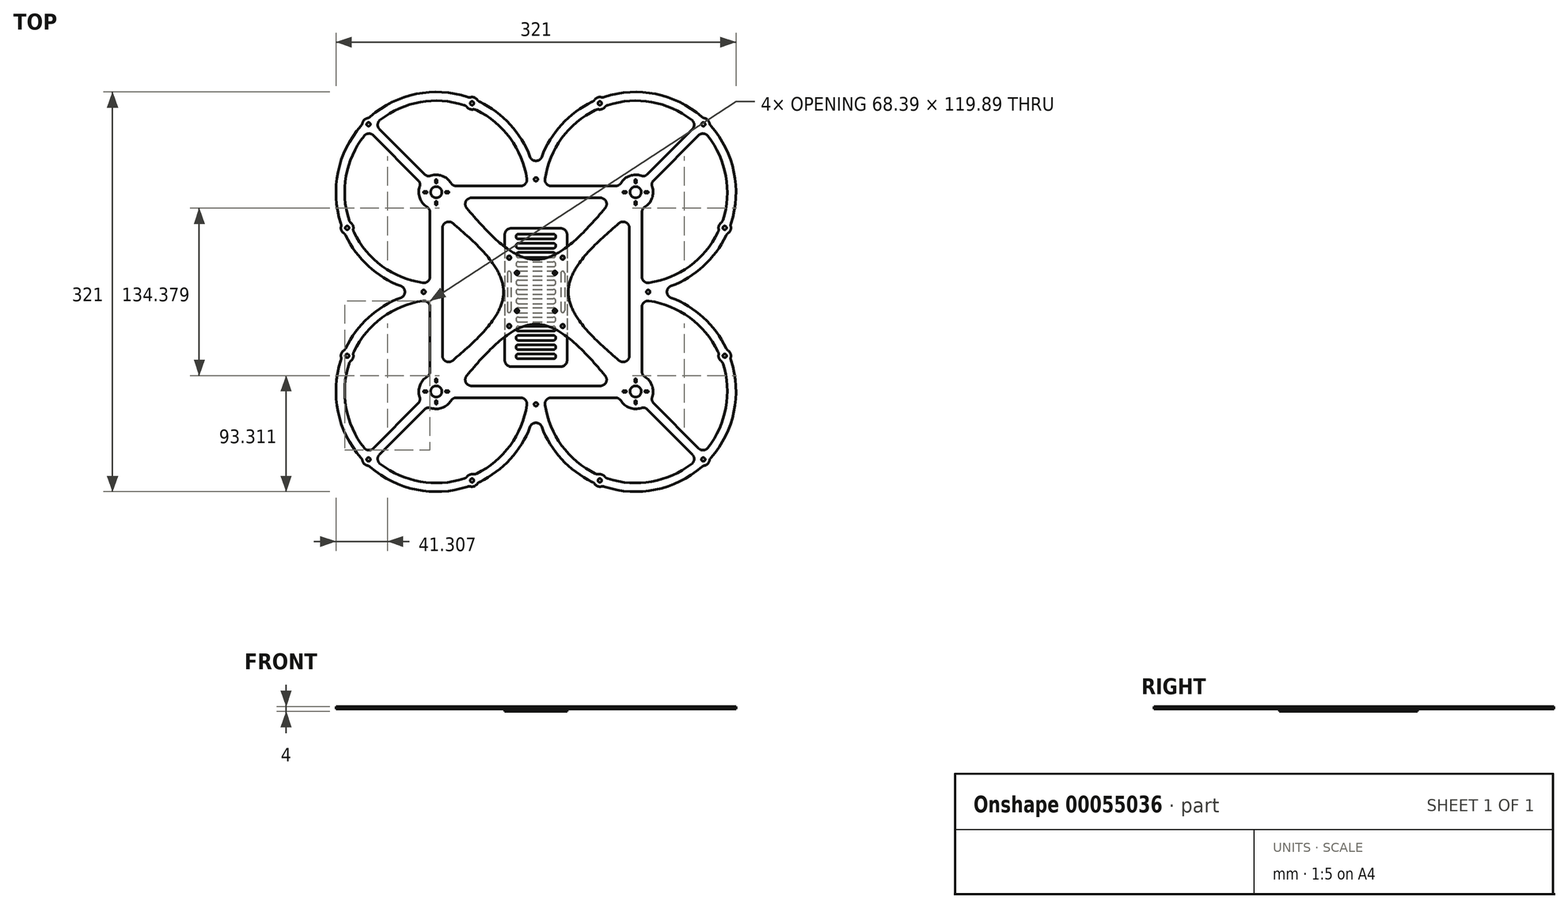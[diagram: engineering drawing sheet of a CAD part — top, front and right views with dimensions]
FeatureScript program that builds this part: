
annotation { "Feature Type Name" : "Feature", "Feature Type Description" : "" }
export const myFeature = defineFeature(function(context is Context, id is Id, definition is map)
    precondition{}
    {
        {
            var Q0;
            Q0=qCreatedBy(makeId("Top.planeOp"),FACE);
            var sketch = newSketch(context, id + "F0", { "sketchPlane" : qUnion([Q0])});
            skPoint(sketch, "E0.rect.middle", {"position": v(0, 0) * mm});
            skArc(sketch, "E1", {"start": v(-68.1, 87.37) * mm, "mid": v(-75.23, 93.16) * mm, "end": v(-84.42, 93.28) * mm});
            skArc(sketch, "E2", {"start": v(87.37, 68.1) * mm, "mid": v(93.16, 75.24) * mm, "end": v(93.28, 84.43) * mm});
            skArc(sketch, "E3", {"start": v(80, -66) * mm, "mid": v(79.97, -66) * mm, "end": v(79.94, -66) * mm});
            skArc(sketch, "E4", {"start": v(-87.37, -68.1) * mm, "mid": v(-93.16, -75.24) * mm, "end": v(-93.28, -84.43) * mm});
            skLineSegment(sketch, "E5.rect.bottom", {"start": v(15.25, -15.25) * mm, "end": v(-15.25, -15.25) * mm, "construction": true});
            skLineSegment(sketch, "E5.rect.top", {"start": v(15.25, 15.25) * mm, "end": v(-15.25, 15.25) * mm, "construction": true});
            skLineSegment(sketch, "E5.rect.left", {"start": v(15.25, -15.25) * mm, "end": v(15.25, 15.25) * mm, "construction": true});
            skLineSegment(sketch, "E5.rect.right", {"start": v(-15.25, -15.25) * mm, "end": v(-15.25, 15.25) * mm, "construction": true});
            skCircle(sketch, "E6", {"center": v(-80, 80) * mm, "radius": 63.5 * mm, "construction": true});
            skCircle(sketch, "E7", {"center": v(80, 80) * mm, "radius": 63.5 * mm, "construction": true});
            skCircle(sketch, "E8", {"center": v(-80, -80) * mm, "radius": 63.5 * mm, "construction": true});
            skCircle(sketch, "E9", {"center": v(80, -80) * mm, "radius": 63.5 * mm, "construction": true});
            skLineSegment(sketch, "E10.rect.bottom", {"start": v(26, -26) * mm, "end": v(-26, -26) * mm});
            skLineSegment(sketch, "E10.rect.top", {"start": v(26, 26) * mm, "end": v(-26, 26) * mm});
            skLineSegment(sketch, "E10.rect.left", {"start": v(26, -26) * mm, "end": v(26, 26) * mm});
            skLineSegment(sketch, "E10.rect.right", {"start": v(-26, -26) * mm, "end": v(-26, 26) * mm});
            skLineSegment(sketch, "E11.0", {"start": v(-85, -63.84) * mm, "end": v(-85, -12.23) * mm});
            skLineSegment(sketch, "E11.1", {"start": v(63.84, -85) * mm, "end": v(12.23, -85) * mm});
            skLineSegment(sketch, "E11.2", {"start": v(85, -63.84) * mm, "end": v(85, -12.23) * mm});
            skLineSegment(sketch, "E11.3", {"start": v(63.84, 85) * mm, "end": v(12.23, 85) * mm});
            skLineSegment(sketch, "E12.0", {"start": v(51.72, 75.5) * mm, "end": v(-51.72, 75.5) * mm});
            skLineSegment(sketch, "E12.1", {"start": v(75, -51.34) * mm, "end": v(75, 51.3) * mm});
            skLineSegment(sketch, "E12.2", {"start": v(51.72, -75.5) * mm, "end": v(-51.72, -75.5) * mm});
            skLineSegment(sketch, "E12.3", {"start": v(-75, -51.3) * mm, "end": v(-75, 51.3) * mm});
            skFitSpline(sketch, "E13", {"points": [v(-66, 80) * mm, v(0, 26) * mm, v(66, 80) * mm], "startDerivative": vector(132, -162) * mm, "endDerivative": vector(132, 162) * mm});
            skFitSpline(sketch, "E14", {"points": [v(-80, 66) * mm, v(-26, 0) * mm, v(-80, -66) * mm], "startDerivative": vector(162, -132) * mm, "endDerivative": vector(-162, -132) * mm});
            skFitSpline(sketch, "E15", {"points": [v(-66, -80) * mm, v(0, -26) * mm, v(66, -80) * mm], "startDerivative": vector(132, 162) * mm, "endDerivative": vector(132, -162) * mm});
            skFitSpline(sketch, "E16", {"points": [v(79.94, -66) * mm, v(26, 0) * mm, v(80, 66) * mm], "startDerivative": vector(-161.86, 132.02) * mm, "endDerivative": vector(161.96, 131.98) * mm});
            skArc(sketch, "E17.trimOffspring", {"start": v(68.1, -87.37) * mm, "mid": v(75.23, -93.16) * mm, "end": v(84.42, -93.28) * mm});
            skPoint(sketch, "E18", {"position": v(0, -124.8) * mm});
            skPoint(sketch, "E19.orphan", {"position": v(0, 114.1) * mm});
            skLineSegment(sketch, "E20.trimOffspring", {"start": v(-85, 12.23) * mm, "end": v(-85, 63.84) * mm});
            skLineSegment(sketch, "E21.trimOffspring", {"start": v(85, 12.23) * mm, "end": v(85, 63.84) * mm});
            skLineSegment(sketch, "E22.trimOffspring", {"start": v(-12.23, -85) * mm, "end": v(-63.84, -85) * mm});
            skLineSegment(sketch, "E23.trimOffspring", {"start": v(-12.23, 85) * mm, "end": v(-63.84, 85) * mm});
            skLineSegment(sketch, "E24", {"start": v(-124.66, 124.8) * mm, "end": v(-125, 125.15) * mm, "construction": true});
            skLineSegment(sketch, "E25", {"start": v(124.66, 124.8) * mm, "end": v(124.83, 124.97) * mm, "construction": true});
            skLineSegment(sketch, "E26", {"start": v(124.66, -124.8) * mm, "end": v(124.83, -124.97) * mm, "construction": true});
            skLineSegment(sketch, "E27", {"start": v(-124.66, -124.8) * mm, "end": v(-124.83, -124.97) * mm, "construction": true});
            skLineSegment(sketch, "E28.0", {"start": v(-94.48, 89.54) * mm, "end": v(-130.46, 125.67) * mm});
            skLineSegment(sketch, "E29.0", {"start": v(94.48, 89.54) * mm, "end": v(130.46, 125.67) * mm});
            skLineSegment(sketch, "E30.0", {"start": v(89.54, -94.5) * mm, "end": v(125.5, -130.61) * mm});
            skLineSegment(sketch, "E31.0", {"start": v(-94.48, -89.54) * mm, "end": v(-130.46, -125.67) * mm});
            skLineSegment(sketch, "E32.0", {"start": v(-89.54, 94.5) * mm, "end": v(-125.5, 130.61) * mm});
            skLineSegment(sketch, "E33.0", {"start": v(89.54, 94.5) * mm, "end": v(125.5, 130.61) * mm});
            skLineSegment(sketch, "E34.0", {"start": v(94.48, -89.54) * mm, "end": v(130.46, -125.67) * mm});
            skLineSegment(sketch, "E35.0", {"start": v(-89.54, -94.5) * mm, "end": v(-125.5, -130.61) * mm});
            skPoint(sketch, "E36.orphan", {"position": v(-89.9, 89.9) * mm});
            skPoint(sketch, "E37.orphan", {"position": v(-133.3, 133.48) * mm});
            skPoint(sketch, "E38.orphan", {"position": v(89.9, 89.9) * mm});
            skPoint(sketch, "E39.orphan", {"position": v(131.88, 132.06) * mm});
            skPoint(sketch, "E40.orphan", {"position": v(89.9, -89.9) * mm});
            skPoint(sketch, "E41.orphan", {"position": v(131.88, -132.06) * mm});
            skPoint(sketch, "E42.orphan", {"position": v(-89.9, -89.9) * mm});
            skPoint(sketch, "E43.orphan", {"position": v(-131.88, -132.06) * mm});
            skLineSegment(sketch, "E44", {"start": v(-87.42, 92.37) * mm, "end": v(-87.11, 92.06) * mm});
            skLineSegment(sketch, "E45", {"start": v(-92.38, 87.43) * mm, "end": v(-92.06, 87.1) * mm});
            skLineSegment(sketch, "E46", {"start": v(87.42, 92.37) * mm, "end": v(87.11, 92.06) * mm});
            skLineSegment(sketch, "E47", {"start": v(92.38, 87.43) * mm, "end": v(92.06, 87.1) * mm});
            skLineSegment(sketch, "E48", {"start": v(92.38, -87.43) * mm, "end": v(92.06, -87.1) * mm});
            skLineSegment(sketch, "E49", {"start": v(87.42, -92.37) * mm, "end": v(87.11, -92.06) * mm});
            skLineSegment(sketch, "E50", {"start": v(-92.38, -87.43) * mm, "end": v(-92.06, -87.1) * mm});
            skLineSegment(sketch, "E51", {"start": v(-87.42, -92.37) * mm, "end": v(-87.11, -92.06) * mm});
            skArc(sketch, "E52.trimOffspring", {"start": v(-93.28, 84.43) * mm, "mid": v(-93.16, 75.24) * mm, "end": v(-87.37, 68.1) * mm});
            skArc(sketch, "E53.filletArc", {"start": v(-89.54, 94.5) * mm, "mid": v(-87.15, 93.16) * mm, "end": v(-84.42, 93.28) * mm});
            skArc(sketch, "E54.trimOffspring", {"start": v(84.42, 93.28) * mm, "mid": v(75.23, 93.16) * mm, "end": v(68.1, 87.37) * mm});
            skArc(sketch, "E55.trimOffspring", {"start": v(93.28, -84.43) * mm, "mid": v(93.16, -75.24) * mm, "end": v(87.37, -68.1) * mm});
            skArc(sketch, "E56.trimOffspring", {"start": v(-84.42, -93.28) * mm, "mid": v(-75.23, -93.16) * mm, "end": v(-68.1, -87.37) * mm});
            skArc(sketch, "E57.filletArc", {"start": v(-93.28, 84.43) * mm, "mid": v(-93.16, 87.16) * mm, "end": v(-94.48, 89.54) * mm});
            skPoint(sketch, "E58.visualSharp", {"position": v(-66.92, 85) * mm});
            skArc(sketch, "E58.filletArc", {"start": v(-68.1, 87.37) * mm, "mid": v(-66.28, 85.63) * mm, "end": v(-63.84, 85) * mm});
            skPoint(sketch, "E59.visualSharp", {"position": v(-85, 66.92) * mm});
            skArc(sketch, "E59.filletArc", {"start": v(-85, 63.84) * mm, "mid": v(-85.63, 66.28) * mm, "end": v(-87.37, 68.1) * mm});
            skPoint(sketch, "E60.visualSharp", {"position": v(-62.33, 75.5) * mm});
            skArc(sketch, "E60.filletArc", {"start": v(-51.72, 75.5) * mm, "mid": v(-56.25, 72.62) * mm, "end": v(-55.56, 67.3) * mm});
            skPoint(sketch, "E61.visualSharp", {"position": v(-75, 61.92) * mm});
            skArc(sketch, "E61.filletArc", {"start": v(-66.79, 55.14) * mm, "mid": v(-72.12, 55.84) * mm, "end": v(-75, 51.3) * mm});
            skArc(sketch, "E62.filletArc", {"start": v(-125.02, 138.1) * mm, "mid": v(-126.95, 134.46) * mm, "end": v(-125.5, 130.61) * mm});
            skArc(sketch, "E63.filletArc", {"start": v(-130.46, 125.67) * mm, "mid": v(-134.3, 127.13) * mm, "end": v(-137.94, 125.22) * mm});
            skPoint(sketch, "E64.visualSharp", {"position": v(-4.93, 114.55) * mm});
            skPoint(sketch, "E65.visualSharp", {"position": v(5, 114.56) * mm});
            skPoint(sketch, "E66.visualSharp", {"position": v(66.92, 85) * mm});
            skArc(sketch, "E66.filletArc", {"start": v(63.84, 85) * mm, "mid": v(66.28, 85.63) * mm, "end": v(68.1, 87.37) * mm});
            skArc(sketch, "E67.filletArc", {"start": v(84.42, 93.28) * mm, "mid": v(87.15, 93.16) * mm, "end": v(89.54, 94.5) * mm});
            skArc(sketch, "E68.filletArc", {"start": v(125.5, 130.61) * mm, "mid": v(126.95, 134.46) * mm, "end": v(125.02, 138.1) * mm});
            skArc(sketch, "E69.filletArc", {"start": v(137.94, 125.22) * mm, "mid": v(134.3, 127.13) * mm, "end": v(130.46, 125.67) * mm});
            skArc(sketch, "E70.filletArc", {"start": v(94.48, 89.54) * mm, "mid": v(93.16, 87.16) * mm, "end": v(93.28, 84.43) * mm});
            skPoint(sketch, "E71.visualSharp", {"position": v(85, 66.92) * mm});
            skArc(sketch, "E71.filletArc", {"start": v(87.37, 68.1) * mm, "mid": v(85.63, 66.28) * mm, "end": v(85, 63.84) * mm});
            skPoint(sketch, "E72.visualSharp", {"position": v(62.33, 75.5) * mm});
            skArc(sketch, "E72.filletArc", {"start": v(55.56, 67.3) * mm, "mid": v(56.25, 72.62) * mm, "end": v(51.72, 75.5) * mm});
            skPoint(sketch, "E73.visualSharp", {"position": v(75, 61.92) * mm});
            skArc(sketch, "E73.filletArc", {"start": v(75, 51.3) * mm, "mid": v(72.12, 55.83) * mm, "end": v(66.79, 55.14) * mm});
            skPoint(sketch, "E74.visualSharp", {"position": v(85, -66.92) * mm});
            skArc(sketch, "E74.filletArc", {"start": v(85, -63.84) * mm, "mid": v(85.63, -66.28) * mm, "end": v(87.37, -68.1) * mm});
            skArc(sketch, "E75.filletArc", {"start": v(93.28, -84.43) * mm, "mid": v(93.16, -87.16) * mm, "end": v(94.48, -89.54) * mm});
            skArc(sketch, "E76.filletArc", {"start": v(130.46, -125.67) * mm, "mid": v(134.3, -127.13) * mm, "end": v(137.94, -125.22) * mm});
            skArc(sketch, "E77.filletArc", {"start": v(125.02, -138.1) * mm, "mid": v(126.95, -134.46) * mm, "end": v(125.5, -130.61) * mm});
            skArc(sketch, "E78.filletArc", {"start": v(89.54, -94.5) * mm, "mid": v(87.15, -93.16) * mm, "end": v(84.42, -93.28) * mm});
            skPoint(sketch, "E79.visualSharp", {"position": v(66.92, -85) * mm});
            skArc(sketch, "E79.filletArc", {"start": v(68.1, -87.37) * mm, "mid": v(66.28, -85.63) * mm, "end": v(63.84, -85) * mm});
            skPoint(sketch, "E80.visualSharp", {"position": v(62.33, -75.5) * mm});
            skArc(sketch, "E80.filletArc", {"start": v(51.72, -75.5) * mm, "mid": v(56.25, -72.62) * mm, "end": v(55.56, -67.3) * mm});
            skPoint(sketch, "E81.visualSharp", {"position": v(75, -61.96) * mm});
            skArc(sketch, "E81.filletArc", {"start": v(66.79, -55.17) * mm, "mid": v(72.11, -55.87) * mm, "end": v(75, -51.34) * mm});
            skPoint(sketch, "E82.visualSharp", {"position": v(-5.02, -114.56) * mm});
            skPoint(sketch, "E83.visualSharp", {"position": v(-66.92, -85) * mm});
            skArc(sketch, "E83.filletArc", {"start": v(-63.84, -85) * mm, "mid": v(-66.28, -85.63) * mm, "end": v(-68.1, -87.37) * mm});
            skArc(sketch, "E84.filletArc", {"start": v(-84.42, -93.28) * mm, "mid": v(-87.15, -93.16) * mm, "end": v(-89.54, -94.5) * mm});
            skArc(sketch, "E85.filletArc", {"start": v(-125.5, -130.61) * mm, "mid": v(-126.95, -134.46) * mm, "end": v(-125.02, -138.1) * mm});
            skArc(sketch, "E86.filletArc", {"start": v(-137.94, -125.22) * mm, "mid": v(-134.3, -127.13) * mm, "end": v(-130.46, -125.67) * mm});
            skArc(sketch, "E87.filletArc", {"start": v(-94.48, -89.54) * mm, "mid": v(-93.16, -87.16) * mm, "end": v(-93.28, -84.43) * mm});
            skPoint(sketch, "E88.visualSharp", {"position": v(-85, -66.92) * mm});
            skArc(sketch, "E88.filletArc", {"start": v(-87.37, -68.1) * mm, "mid": v(-85.63, -66.28) * mm, "end": v(-85, -63.84) * mm});
            skPoint(sketch, "E89.visualSharp", {"position": v(-62.33, -75.5) * mm});
            skArc(sketch, "E89.filletArc", {"start": v(-55.56, -67.3) * mm, "mid": v(-56.25, -72.62) * mm, "end": v(-51.72, -75.5) * mm});
            skPoint(sketch, "E90.visualSharp", {"position": v(-75, -61.92) * mm});
            skArc(sketch, "E90.filletArc", {"start": v(-75, -51.3) * mm, "mid": v(-72.12, -55.84) * mm, "end": v(-66.79, -55.14) * mm});
            skArc(sketch, "E91", {"start": v(33.54, -16.78) * mm, "mid": v(37.5, 0) * mm, "end": v(33.54, 16.77) * mm});
            skFitSpline(sketch, "E92.trimOffspring", {"points": [v(-66, -80) * mm, v(0, -26) * mm, v(66, -80) * mm], "startDerivative": vector(132, 162) * mm, "endDerivative": vector(132, -162) * mm});
            skArc(sketch, "E93.trimOffspring", {"start": v(-16.77, -33.54) * mm, "mid": v(0, -37.5) * mm, "end": v(16.77, -33.54) * mm});
            skFitSpline(sketch, "E94.trimOffspring", {"points": [v(-80, 66) * mm, v(-26, 0) * mm, v(-80, -66) * mm], "startDerivative": vector(162, -132) * mm, "endDerivative": vector(-162, -132) * mm});
            skArc(sketch, "E95.trimOffspring", {"start": v(-33.54, 16.77) * mm, "mid": v(-37.5, 0) * mm, "end": v(-33.54, -16.77) * mm});
            skArc(sketch, "E96.trimOffspring", {"start": v(16.77, 33.54) * mm, "mid": v(0, 37.5) * mm, "end": v(-16.77, 33.54) * mm});
            skPoint(sketch, "E97.visualSharp", {"position": v(-19.22, 32.2) * mm});
            skArc(sketch, "E97.filletArc", {"start": v(-21.81, 33.87) * mm, "mid": v(-19.34, 33.02) * mm, "end": v(-16.77, 33.54) * mm});
            skPoint(sketch, "E98.visualSharp", {"position": v(19.22, 32.2) * mm});
            skArc(sketch, "E98.filletArc", {"start": v(16.77, 33.54) * mm, "mid": v(19.34, 33.02) * mm, "end": v(21.81, 33.87) * mm});
            skPoint(sketch, "E99.visualSharp", {"position": v(32.2, 19.22) * mm});
            skArc(sketch, "E99.filletArc", {"start": v(33.87, 21.8) * mm, "mid": v(33.02, 19.34) * mm, "end": v(33.54, 16.77) * mm});
            skPoint(sketch, "E100.visualSharp", {"position": v(32.2, -19.23) * mm});
            skArc(sketch, "E100.filletArc", {"start": v(33.54, -16.78) * mm, "mid": v(33.02, -19.34) * mm, "end": v(33.87, -21.82) * mm});
            skPoint(sketch, "E101.visualSharp", {"position": v(19.22, -32.2) * mm});
            skArc(sketch, "E101.filletArc", {"start": v(21.81, -33.87) * mm, "mid": v(19.34, -33.02) * mm, "end": v(16.77, -33.54) * mm});
            skPoint(sketch, "E102.visualSharp", {"position": v(-19.22, -32.2) * mm});
            skArc(sketch, "E102.filletArc", {"start": v(-16.77, -33.54) * mm, "mid": v(-19.34, -33.02) * mm, "end": v(-21.81, -33.87) * mm});
            skPoint(sketch, "E103.visualSharp", {"position": v(-32.2, -19.22) * mm});
            skArc(sketch, "E103.filletArc", {"start": v(-33.87, -21.81) * mm, "mid": v(-33.02, -19.34) * mm, "end": v(-33.54, -16.77) * mm});
            skPoint(sketch, "E104.visualSharp", {"position": v(-32.2, 19.22) * mm});
            skArc(sketch, "E104.filletArc", {"start": v(-33.54, 16.77) * mm, "mid": v(-33.02, 19.34) * mm, "end": v(-33.87, 21.81) * mm});
            skCircle(sketch, "E105", {"center": v(15.25, -15.25) * mm, "radius": 1.5 * mm});
            skCircle(sketch, "E106", {"center": v(-15.25, -15.25) * mm, "radius": 1.5 * mm});
            skCircle(sketch, "E107", {"center": v(-15.25, 15.25) * mm, "radius": 1.5 * mm});
            skCircle(sketch, "E108", {"center": v(15.25, 15.25) * mm, "radius": 1.5 * mm});
            skCircle(sketch, "E109", {"center": v(32.2, 0) * mm, "radius": 1.5 * mm});
            skCircle(sketch, "E110", {"center": v(0, -32.2) * mm, "radius": 1.5 * mm});
            skLineSegment(sketch, "E111", {"start": v(0, -141.51) * mm, "end": v(0, 75.5) * mm, "construction": true});
            skLineSegment(sketch, "E112", {"start": v(141.95, 0) * mm, "end": v(-75, 0) * mm, "construction": true});
            skCircle(sketch, "E113.MirrorC", {"center": v(-32.2, 0) * mm, "radius": 1.5 * mm});
            skCircle(sketch, "E114.MirrorC", {"center": v(0, 32.2) * mm, "radius": 1.5 * mm});
            skArc(sketch, "E115.filletArc", {"start": v(12.23, -85) * mm, "mid": v(8.45, -86.73) * mm, "end": v(7.29, -90.73) * mm});
            skArc(sketch, "E116.filletArc", {"start": v(-7.29, -90.73) * mm, "mid": v(-8.45, -86.73) * mm, "end": v(-12.23, -85) * mm});
            skArc(sketch, "E117.filletArc", {"start": v(4.68, -108.4) * mm, "mid": v(0, -105.17) * mm, "end": v(-4.68, -108.4) * mm});
            skPoint(sketch, "E118.visualSharp", {"position": v(6.67, 85) * mm});
            skArc(sketch, "E118.filletArc", {"start": v(7.29, 90.73) * mm, "mid": v(8.45, 86.73) * mm, "end": v(12.23, 85) * mm});
            skPoint(sketch, "E119.visualSharp", {"position": v(-6.67, 85) * mm});
            skArc(sketch, "E119.filletArc", {"start": v(-12.23, 85) * mm, "mid": v(-8.45, 86.73) * mm, "end": v(-7.29, 90.73) * mm});
            skPoint(sketch, "E120.visualSharp", {"position": v(0, 88.96) * mm});
            skArc(sketch, "E120.filletArc", {"start": v(-4.68, 108.4) * mm, "mid": v(0, 105.17) * mm, "end": v(4.68, 108.4) * mm});
            skArc(sketch, "E121.filletArc", {"start": v(-85, -12.23) * mm, "mid": v(-86.73, -8.45) * mm, "end": v(-90.73, -7.29) * mm});
            skArc(sketch, "E122.filletArc", {"start": v(-90.73, 7.29) * mm, "mid": v(-86.73, 8.45) * mm, "end": v(-85, 12.23) * mm});
            skPoint(sketch, "E123.visualSharp", {"position": v(-88.96, 0) * mm});
            skArc(sketch, "E123.filletArc", {"start": v(-108.4, -4.68) * mm, "mid": v(-105.17, 0) * mm, "end": v(-108.4, 4.68) * mm});
            skPoint(sketch, "E124.visualSharp", {"position": v(85, -6.67) * mm});
            skArc(sketch, "E124.filletArc", {"start": v(90.73, -7.29) * mm, "mid": v(86.73, -8.45) * mm, "end": v(85, -12.23) * mm});
            skPoint(sketch, "E125.visualSharp", {"position": v(85, 6.67) * mm});
            skArc(sketch, "E125.filletArc", {"start": v(85, 12.23) * mm, "mid": v(86.73, 8.45) * mm, "end": v(90.73, 7.29) * mm});
            skArc(sketch, "E126.filletArc", {"start": v(108.4, 4.68) * mm, "mid": v(105.17, 0) * mm, "end": v(108.4, -4.68) * mm});
            skArc(sketch, "E127", {"start": v(-90.73, 7.29) * mm, "mid": v(-123.42, 20.7) * mm, "end": v(-146.07, 47.8) * mm});
            skArc(sketch, "E128", {"start": v(-108.4, 4.68) * mm, "mid": v(-134.45, 20.7) * mm, "end": v(-152.63, 45.3) * mm});
            skArc(sketch, "E129", {"start": v(-7.29, 90.73) * mm, "mid": v(-20.66, 123.37) * mm, "end": v(-47.7, 146.02) * mm});
            skLineSegment(sketch, "E130", {"start": v(-138.95, 56.4) * mm, "end": v(-148.23, 52.68) * mm, "construction": true});
            skLineSegment(sketch, "E131", {"start": v(-148.23, 52.68) * mm, "end": v(-160.6, 47.73) * mm, "construction": true});
            skLineSegment(sketch, "E132", {"start": v(-52.57, 148.19) * mm, "end": v(-48.09, 159.32) * mm, "construction": true});
            skCircle(sketch, "E133", {"center": v(-80, 80) * mm, "radius": 77 * mm, "construction": true});
            skArc(sketch, "E134", {"start": v(-156.38, 52.4) * mm, "mid": v(-156.13, 49.52) * mm, "end": v(-154.31, 47.26) * mm});
            skArc(sketch, "E135", {"start": v(-55.18, 148.34) * mm, "mid": v(-53.13, 146.8) * mm, "end": v(-50.58, 146.48) * mm});
            skArc(sketch, "E136.trimOffspring", {"start": v(-47.14, 154.26) * mm, "mid": v(-49.4, 156.07) * mm, "end": v(-52.28, 156.33) * mm});
            skArc(sketch, "E137.trimOffspring", {"start": v(-45.17, 152.58) * mm, "mid": v(-20.66, 134.4) * mm, "end": v(-4.68, 108.4) * mm});
            skArc(sketch, "E138.trimOffspring", {"start": v(-57.58, 150) * mm, "mid": v(-92.77, 152.38) * mm, "end": v(-125.02, 138.1) * mm});
            skPoint(sketch, "E139.visualSharp", {"position": v(-46.6, 153.24) * mm});
            skArc(sketch, "E139.filletArc", {"start": v(-47.14, 154.26) * mm, "mid": v(-46.26, 153.29) * mm, "end": v(-45.17, 152.58) * mm});
            skPoint(sketch, "E140.visualSharp", {"position": v(-49.36, 146.81) * mm});
            skArc(sketch, "E140.filletArc", {"start": v(-47.7, 146.02) * mm, "mid": v(-49.1, 146.47) * mm, "end": v(-50.58, 146.48) * mm});
            skPoint(sketch, "E141.visualSharp", {"position": v(-55.83, 149.41) * mm});
            skArc(sketch, "E141.filletArc", {"start": v(-55.18, 148.34) * mm, "mid": v(-56.26, 149.35) * mm, "end": v(-57.58, 150) * mm});
            skPoint(sketch, "E142.visualSharp", {"position": v(-53.37, 155.97) * mm});
            skArc(sketch, "E142.filletArc", {"start": v(-54.86, 156.48) * mm, "mid": v(-53.58, 156.23) * mm, "end": v(-52.28, 156.33) * mm});
            skArc(sketch, "E143.trimOffspring", {"start": v(-156.52, 55) * mm, "mid": v(-158.84, 96.26) * mm, "end": v(-140.38, 133.24) * mm});
            skArc(sketch, "E144.trimOffspring", {"start": v(-150.04, 57.7) * mm, "mid": v(-152.35, 92.96) * mm, "end": v(-137.94, 125.22) * mm});
            skArc(sketch, "E145.trimOffspring", {"start": v(-146.53, 50.69) * mm, "mid": v(-146.84, 53.24) * mm, "end": v(-148.38, 55.3) * mm});
            skPoint(sketch, "E146.visualSharp", {"position": v(-153.3, 46.72) * mm});
            skArc(sketch, "E146.filletArc", {"start": v(-152.63, 45.3) * mm, "mid": v(-153.35, 46.39) * mm, "end": v(-154.31, 47.26) * mm});
            skPoint(sketch, "E147.visualSharp", {"position": v(-146.86, 49.47) * mm});
            skArc(sketch, "E147.filletArc", {"start": v(-146.53, 50.69) * mm, "mid": v(-146.52, 49.21) * mm, "end": v(-146.07, 47.8) * mm});
            skPoint(sketch, "E148.visualSharp", {"position": v(-149.45, 55.95) * mm});
            skArc(sketch, "E148.filletArc", {"start": v(-150.04, 57.7) * mm, "mid": v(-149.39, 56.38) * mm, "end": v(-148.38, 55.3) * mm});
            skPoint(sketch, "E149.visualSharp", {"position": v(-156.01, 53.5) * mm});
            skArc(sketch, "E149.filletArc", {"start": v(-156.38, 52.4) * mm, "mid": v(-156.28, 53.71) * mm, "end": v(-156.52, 55) * mm});
            skCircle(sketch, "E150", {"center": v(-151.48, 51.38) * mm, "radius": 1.5 * mm});
            skCircle(sketch, "E151", {"center": v(-51.26, 151.44) * mm, "radius": 1.5 * mm});
            skArc(sketch, "E152", {"start": v(7.29, 90.73) * mm, "mid": v(20.66, 123.37) * mm, "end": v(47.7, 146.02) * mm});
            skArc(sketch, "E153", {"start": v(137.94, 125.22) * mm, "mid": v(152.35, 92.96) * mm, "end": v(150.04, 57.7) * mm});
            skArc(sketch, "E154", {"start": v(4.68, 108.4) * mm, "mid": v(20.66, 134.4) * mm, "end": v(45.17, 152.58) * mm});
            skArc(sketch, "E155", {"start": v(90.73, -7.29) * mm, "mid": v(123.42, -20.7) * mm, "end": v(146.07, -47.8) * mm});
            skArc(sketch, "E156", {"start": v(125.02, -138.1) * mm, "mid": v(92.77, -152.38) * mm, "end": v(57.58, -150) * mm});
            skArc(sketch, "E157", {"start": v(108.4, -4.68) * mm, "mid": v(134.45, -20.7) * mm, "end": v(152.63, -45.3) * mm});
            skArc(sketch, "E158", {"start": v(-90.73, -7.29) * mm, "mid": v(-123.42, -20.7) * mm, "end": v(-146.07, -47.8) * mm});
            skArc(sketch, "E159", {"start": v(-125.02, -138.1) * mm, "mid": v(-92.77, -152.38) * mm, "end": v(-57.58, -150) * mm});
            skArc(sketch, "E160", {"start": v(-108.4, -4.68) * mm, "mid": v(-134.45, -20.7) * mm, "end": v(-152.63, -45.3) * mm});
            skArc(sketch, "E161.MirrorCS", {"start": v(47.14, 154.26) * mm, "mid": v(49.4, 156.07) * mm, "end": v(52.28, 156.33) * mm});
            skArc(sketch, "E162.MirrorCS", {"start": v(55.18, 148.34) * mm, "mid": v(53.13, 146.8) * mm, "end": v(50.58, 146.48) * mm});
            skCircle(sketch, "E163.MirrorC", {"center": v(51.26, 151.44) * mm, "radius": 1.5 * mm});
            skArc(sketch, "E164.MirrorCS", {"start": v(55.18, 148.34) * mm, "mid": v(56.26, 149.35) * mm, "end": v(57.58, 150) * mm});
            skArc(sketch, "E165.MirrorCS", {"start": v(47.7, 146.02) * mm, "mid": v(49.1, 146.47) * mm, "end": v(50.58, 146.48) * mm});
            skArc(sketch, "E166.MirrorCS", {"start": v(47.14, 154.26) * mm, "mid": v(46.26, 153.29) * mm, "end": v(45.17, 152.58) * mm});
            skArc(sketch, "E167.MirrorCS", {"start": v(54.86, 156.48) * mm, "mid": v(53.58, 156.23) * mm, "end": v(52.28, 156.33) * mm});
            skCircle(sketch, "E168.MirrorC", {"center": v(151.48, 51.38) * mm, "radius": 1.5 * mm});
            skArc(sketch, "E169.MirrorCS", {"start": v(146.53, 50.69) * mm, "mid": v(146.84, 53.24) * mm, "end": v(148.38, 55.3) * mm});
            skArc(sketch, "E170.MirrorCS", {"start": v(156.38, 52.4) * mm, "mid": v(156.13, 49.52) * mm, "end": v(154.31, 47.26) * mm});
            skArc(sketch, "E171.MirrorCS", {"start": v(156.38, 52.4) * mm, "mid": v(156.28, 53.71) * mm, "end": v(156.52, 55) * mm});
            skArc(sketch, "E172.MirrorCS", {"start": v(150.04, 57.7) * mm, "mid": v(149.39, 56.38) * mm, "end": v(148.38, 55.3) * mm});
            skArc(sketch, "E173.MirrorCS", {"start": v(146.53, 50.69) * mm, "mid": v(146.52, 49.21) * mm, "end": v(146.07, 47.8) * mm});
            skArc(sketch, "E174.MirrorCS", {"start": v(152.63, 45.3) * mm, "mid": v(153.35, 46.39) * mm, "end": v(154.31, 47.26) * mm});
            skLineSegment(sketch, "E175", {"start": v(-80, 80) * mm, "end": v(-139.42, 139.67) * mm, "construction": true});
            skArc(sketch, "E176", {"start": v(-135.3, 139.47) * mm, "mid": v(-137.86, 138.1) * mm, "end": v(-139.23, 135.55) * mm});
            skCircle(sketch, "E177", {"center": v(-134.33, 134.56) * mm, "radius": 1.5 * mm});
            skArc(sketch, "E178.trimOffspring", {"start": v(-132.98, 140.6) * mm, "mid": v(-96.03, 158.89) * mm, "end": v(-54.86, 156.48) * mm});
            skPoint(sketch, "E179.visualSharp", {"position": v(-139.33, 134.4) * mm});
            skArc(sketch, "E179.filletArc", {"start": v(-140.38, 133.24) * mm, "mid": v(-139.66, 134.32) * mm, "end": v(-139.23, 135.55) * mm});
            skPoint(sketch, "E180.visualSharp", {"position": v(-134.16, 139.56) * mm});
            skArc(sketch, "E180.filletArc", {"start": v(-135.3, 139.47) * mm, "mid": v(-134.07, 139.88) * mm, "end": v(-132.98, 140.6) * mm});
            skCircle(sketch, "E181.MirrorC", {"center": v(134.33, 134.56) * mm, "radius": 1.5 * mm});
            skArc(sketch, "E182.MirrorCS", {"start": v(135.3, 139.47) * mm, "mid": v(137.86, 138.1) * mm, "end": v(139.23, 135.55) * mm});
            skArc(sketch, "E183.MirrorCS", {"start": v(135.3, 139.47) * mm, "mid": v(134.07, 139.88) * mm, "end": v(132.98, 140.6) * mm});
            skArc(sketch, "E184.MirrorCS", {"start": v(140.38, 133.24) * mm, "mid": v(139.66, 134.32) * mm, "end": v(139.23, 135.55) * mm});
            skArc(sketch, "E185.trimOffspring", {"start": v(54.86, 156.48) * mm, "mid": v(96.03, 158.89) * mm, "end": v(132.98, 140.6) * mm});
            skArc(sketch, "E186.trimOffspring", {"start": v(57.58, 150) * mm, "mid": v(92.77, 152.38) * mm, "end": v(125.02, 138.1) * mm});
            skArc(sketch, "E187.trimOffspring", {"start": v(140.38, 133.24) * mm, "mid": v(158.84, 96.26) * mm, "end": v(156.52, 55) * mm});
            skArc(sketch, "E188.trimOffspring", {"start": v(146.07, 47.8) * mm, "mid": v(123.42, 20.7) * mm, "end": v(90.73, 7.29) * mm});
            skArc(sketch, "E189.trimOffspring", {"start": v(152.63, 45.3) * mm, "mid": v(134.45, 20.7) * mm, "end": v(108.4, 4.68) * mm});
            skArc(sketch, "E190.MirrorCS", {"start": v(-156.38, -52.4) * mm, "mid": v(-156.28, -53.71) * mm, "end": v(-156.52, -55) * mm});
            skArc(sketch, "E191.MirrorCS", {"start": v(-156.38, -52.4) * mm, "mid": v(-156.13, -49.52) * mm, "end": v(-154.31, -47.26) * mm});
            skArc(sketch, "E192.MirrorCS", {"start": v(-152.63, -45.3) * mm, "mid": v(-153.35, -46.39) * mm, "end": v(-154.31, -47.26) * mm});
            skArc(sketch, "E193.MirrorCS", {"start": v(-150.04, -57.7) * mm, "mid": v(-149.39, -56.38) * mm, "end": v(-148.38, -55.3) * mm});
            skArc(sketch, "E194.MirrorCS", {"start": v(-146.53, -50.69) * mm, "mid": v(-146.84, -53.24) * mm, "end": v(-148.38, -55.3) * mm});
            skArc(sketch, "E195.MirrorCS", {"start": v(-146.53, -50.69) * mm, "mid": v(-146.52, -49.21) * mm, "end": v(-146.07, -47.8) * mm});
            skArc(sketch, "E196.MirrorCS", {"start": v(-135.3, -139.47) * mm, "mid": v(-137.86, -138.1) * mm, "end": v(-139.23, -135.55) * mm});
            skArc(sketch, "E197.MirrorCS", {"start": v(-135.3, -139.47) * mm, "mid": v(-134.07, -139.88) * mm, "end": v(-132.98, -140.6) * mm});
            skArc(sketch, "E198.MirrorCS", {"start": v(-140.38, -133.24) * mm, "mid": v(-139.66, -134.32) * mm, "end": v(-139.23, -135.55) * mm});
            skArc(sketch, "E199.MirrorCS", {"start": v(-54.86, -156.48) * mm, "mid": v(-53.58, -156.23) * mm, "end": v(-52.28, -156.33) * mm});
            skArc(sketch, "E200.MirrorCS", {"start": v(-47.14, -154.26) * mm, "mid": v(-49.4, -156.07) * mm, "end": v(-52.28, -156.33) * mm});
            skArc(sketch, "E201.MirrorCS", {"start": v(-47.7, -146.02) * mm, "mid": v(-49.1, -146.47) * mm, "end": v(-50.58, -146.48) * mm});
            skArc(sketch, "E202.MirrorCS", {"start": v(-55.18, -148.34) * mm, "mid": v(-53.13, -146.8) * mm, "end": v(-50.58, -146.48) * mm});
            skArc(sketch, "E203.MirrorCS", {"start": v(-55.18, -148.34) * mm, "mid": v(-56.26, -149.35) * mm, "end": v(-57.58, -150) * mm});
            skArc(sketch, "E204.MirrorCS", {"start": v(47.14, -154.26) * mm, "mid": v(46.26, -153.29) * mm, "end": v(45.17, -152.58) * mm});
            skArc(sketch, "E205.MirrorCS", {"start": v(47.14, -154.26) * mm, "mid": v(49.4, -156.07) * mm, "end": v(52.28, -156.33) * mm});
            skArc(sketch, "E206.MirrorCS", {"start": v(54.86, -156.48) * mm, "mid": v(53.58, -156.23) * mm, "end": v(52.28, -156.33) * mm});
            skArc(sketch, "E207.MirrorCS", {"start": v(55.18, -148.34) * mm, "mid": v(56.26, -149.35) * mm, "end": v(57.58, -150) * mm});
            skArc(sketch, "E208.MirrorCS", {"start": v(55.18, -148.34) * mm, "mid": v(53.13, -146.8) * mm, "end": v(50.58, -146.48) * mm});
            skArc(sketch, "E209.MirrorCS", {"start": v(47.7, -146.02) * mm, "mid": v(49.1, -146.47) * mm, "end": v(50.58, -146.48) * mm});
            skCircle(sketch, "E210.MirrorC", {"center": v(51.26, -151.44) * mm, "radius": 1.5 * mm});
            skCircle(sketch, "E211.MirrorC", {"center": v(-51.26, -151.44) * mm, "radius": 1.5 * mm});
            skCircle(sketch, "E212.MirrorC", {"center": v(-134.33, -134.56) * mm, "radius": 1.5 * mm});
            skCircle(sketch, "E213.MirrorC", {"center": v(-151.48, -51.38) * mm, "radius": 1.5 * mm});
            skCircle(sketch, "E214.MirrorC", {"center": v(151.48, -51.38) * mm, "radius": 1.5 * mm});
            skArc(sketch, "E215.MirrorCS", {"start": v(150.04, -57.7) * mm, "mid": v(149.39, -56.38) * mm, "end": v(148.38, -55.3) * mm});
            skArc(sketch, "E216.MirrorCS", {"start": v(146.53, -50.69) * mm, "mid": v(146.84, -53.24) * mm, "end": v(148.38, -55.3) * mm});
            skArc(sketch, "E217.MirrorCS", {"start": v(146.53, -50.69) * mm, "mid": v(146.52, -49.21) * mm, "end": v(146.07, -47.8) * mm});
            skArc(sketch, "E218.MirrorCS", {"start": v(156.38, -52.4) * mm, "mid": v(156.28, -53.71) * mm, "end": v(156.52, -55) * mm});
            skArc(sketch, "E219.MirrorCS", {"start": v(156.38, -52.4) * mm, "mid": v(156.13, -49.52) * mm, "end": v(154.31, -47.26) * mm});
            skArc(sketch, "E220.MirrorCS", {"start": v(152.63, -45.3) * mm, "mid": v(153.35, -46.39) * mm, "end": v(154.31, -47.26) * mm});
            skCircle(sketch, "E221.MirrorC", {"center": v(134.33, -134.56) * mm, "radius": 1.5 * mm});
            skArc(sketch, "E222.MirrorCS", {"start": v(135.3, -139.47) * mm, "mid": v(134.07, -139.88) * mm, "end": v(132.98, -140.6) * mm});
            skArc(sketch, "E223.MirrorCS", {"start": v(135.3, -139.47) * mm, "mid": v(137.86, -138.1) * mm, "end": v(139.23, -135.55) * mm});
            skArc(sketch, "E224.MirrorCS", {"start": v(140.38, -133.24) * mm, "mid": v(139.66, -134.32) * mm, "end": v(139.23, -135.55) * mm});
            skArc(sketch, "E225.trimOffspring", {"start": v(150.04, -57.7) * mm, "mid": v(152.35, -92.96) * mm, "end": v(137.94, -125.22) * mm});
            skArc(sketch, "E226.trimOffspring", {"start": v(156.52, -55) * mm, "mid": v(158.84, -96.26) * mm, "end": v(140.38, -133.24) * mm});
            skArc(sketch, "E227.trimOffspring", {"start": v(132.98, -140.6) * mm, "mid": v(96.03, -158.89) * mm, "end": v(54.86, -156.48) * mm});
            skArc(sketch, "E228.trimOffspring", {"start": v(45.17, -152.58) * mm, "mid": v(20.66, -134.4) * mm, "end": v(4.68, -108.4) * mm});
            skArc(sketch, "E229.trimOffspring", {"start": v(47.7, -146.02) * mm, "mid": v(20.66, -123.37) * mm, "end": v(7.29, -90.73) * mm});
            skArc(sketch, "E230.trimOffspring", {"start": v(-47.7, -146.02) * mm, "mid": v(-20.66, -123.37) * mm, "end": v(-7.29, -90.73) * mm});
            skArc(sketch, "E231.MirrorCS", {"start": v(-47.14, -154.26) * mm, "mid": v(-46.26, -153.29) * mm, "end": v(-45.17, -152.58) * mm});
            skArc(sketch, "E232.trimOffspring", {"start": v(-45.17, -152.58) * mm, "mid": v(-20.66, -134.4) * mm, "end": v(-4.68, -108.4) * mm});
            skArc(sketch, "E233.trimOffspring", {"start": v(-132.98, -140.6) * mm, "mid": v(-96.03, -158.89) * mm, "end": v(-54.86, -156.48) * mm});
            skArc(sketch, "E234.trimOffspring", {"start": v(-156.52, -55) * mm, "mid": v(-158.84, -96.26) * mm, "end": v(-140.38, -133.24) * mm});
            skArc(sketch, "E235.trimOffspring", {"start": v(-150.04, -57.7) * mm, "mid": v(-152.35, -92.96) * mm, "end": v(-137.94, -125.22) * mm});
            skLineSegment(sketch, "E236.trimOffspring", {"start": v(-75, 0) * mm, "end": v(141.95, 0) * mm, "construction": true});
            skPoint(sketch, "E237.MirrorCS.start.orphan", {"position": v(-141.95, 0) * mm});
            skLineSegment(sketch, "E238.trimOffspring", {"start": v(-105.17, 0) * mm, "end": v(-110.17, 0) * mm, "construction": true});
            skCircle(sketch, "E239", {"center": v(-90.09, 0) * mm, "radius": 1.5 * mm});
            skLineSegment(sketch, "E240.trimOffspring", {"start": v(0, 105.17) * mm, "end": v(0, 141.51) * mm, "construction": true});
            skCircle(sketch, "E241", {"center": v(0, 90.34) * mm, "radius": 1.5 * mm});
            skCircle(sketch, "E242.MirrorC", {"center": v(0, -90.34) * mm, "radius": 1.5 * mm});
            skCircle(sketch, "E243.MirrorC", {"center": v(90.09, 0) * mm, "radius": 1.5 * mm});
            skLineSegment(sketch, "E244.trimOffspring", {"start": v(-56.3, 138.91) * mm, "end": v(-52.57, 148.19) * mm, "construction": true});
            skCircle(sketch, "E245", {"center": v(-80, 80) * mm, "radius": 4.5 * mm});
            skCircle(sketch, "E246", {"center": v(80, 80) * mm, "radius": 4.5 * mm});
            skCircle(sketch, "E247", {"center": v(80, -80) * mm, "radius": 4.5 * mm});
            skCircle(sketch, "E248", {"center": v(-80, -80) * mm, "radius": 4.5 * mm});
            skCircle(sketch, "E249", {"center": v(-80, 80) * mm, "radius": 9.5 * mm, "construction": true});
            skCircle(sketch, "E250", {"center": v(-80, 80) * mm, "radius": 8 * mm, "construction": true});
            skLineSegment(sketch, "E251", {"start": v(-88, 80) * mm, "end": v(-89.5, 80) * mm});
            skLineSegment(sketch, "E252", {"start": v(-72, 80) * mm, "end": v(-70.5, 80) * mm});
            skLineSegment(sketch, "E253", {"start": v(-80, 88) * mm, "end": v(-80, 89.5) * mm});
            skLineSegment(sketch, "E254", {"start": v(-80, 72) * mm, "end": v(-80, 70.5) * mm});
            skArc(sketch, "E255.0.startCap", {"start": v(-79.25, 88) * mm, "mid": v(-80, 87.25) * mm, "end": v(-80.75, 88) * mm});
            skArc(sketch, "E255.0.endCap", {"start": v(-80.75, 89.5) * mm, "mid": v(-80, 90.25) * mm, "end": v(-79.25, 89.5) * mm});
            skLineSegment(sketch, "E255.0.left", {"start": v(-80.75, 88) * mm, "end": v(-80.75, 89.5) * mm});
            skLineSegment(sketch, "E255.0.right", {"start": v(-79.25, 88) * mm, "end": v(-79.25, 89.5) * mm});
            skArc(sketch, "E256.0.startCap", {"start": v(-72, 79.25) * mm, "mid": v(-72.75, 80) * mm, "end": v(-72, 80.75) * mm});
            skArc(sketch, "E256.0.endCap", {"start": v(-70.5, 80.75) * mm, "mid": v(-69.75, 80) * mm, "end": v(-70.5, 79.25) * mm});
            skLineSegment(sketch, "E256.0.left", {"start": v(-72, 80.75) * mm, "end": v(-70.5, 80.75) * mm});
            skLineSegment(sketch, "E256.0.right", {"start": v(-72, 79.25) * mm, "end": v(-70.5, 79.25) * mm});
            skArc(sketch, "E257.0.startCap", {"start": v(-80.75, 72) * mm, "mid": v(-80, 72.75) * mm, "end": v(-79.25, 72) * mm});
            skArc(sketch, "E257.0.endCap", {"start": v(-79.25, 70.5) * mm, "mid": v(-80, 69.75) * mm, "end": v(-80.75, 70.5) * mm});
            skLineSegment(sketch, "E257.0.left", {"start": v(-79.25, 72) * mm, "end": v(-79.25, 70.5) * mm});
            skLineSegment(sketch, "E257.0.right", {"start": v(-80.75, 72) * mm, "end": v(-80.75, 70.5) * mm});
            skArc(sketch, "E257.1.startCap", {"start": v(-88, 80.75) * mm, "mid": v(-87.25, 80) * mm, "end": v(-88, 79.25) * mm});
            skArc(sketch, "E257.1.endCap", {"start": v(-89.5, 79.25) * mm, "mid": v(-90.25, 80) * mm, "end": v(-89.5, 80.75) * mm});
            skLineSegment(sketch, "E257.1.left", {"start": v(-88, 79.25) * mm, "end": v(-89.5, 79.25) * mm});
            skLineSegment(sketch, "E257.1.right", {"start": v(-88, 80.75) * mm, "end": v(-89.5, 80.75) * mm});
            skArc(sketch, "E258.MirrorCS", {"start": v(79.25, 88) * mm, "mid": v(80, 87.25) * mm, "end": v(80.75, 88) * mm});
            skArc(sketch, "E259.MirrorCS", {"start": v(80.75, 89.5) * mm, "mid": v(80, 90.25) * mm, "end": v(79.25, 89.5) * mm});
            skLineSegment(sketch, "E260.MirrorCS", {"start": v(80.75, 88) * mm, "end": v(80.75, 89.5) * mm});
            skLineSegment(sketch, "E261.MirrorCS", {"start": v(79.25, 88) * mm, "end": v(79.25, 89.5) * mm});
            skLineSegment(sketch, "E262.MirrorCS", {"start": v(72, 79.25) * mm, "end": v(70.5, 79.25) * mm});
            skLineSegment(sketch, "E263.MirrorCS", {"start": v(72, 80.75) * mm, "end": v(70.5, 80.75) * mm});
            skArc(sketch, "E264.MirrorCS", {"start": v(70.5, 80.75) * mm, "mid": v(69.75, 80) * mm, "end": v(70.5, 79.25) * mm});
            skArc(sketch, "E265.MirrorCS", {"start": v(72, 79.25) * mm, "mid": v(72.75, 80) * mm, "end": v(72, 80.75) * mm});
            skArc(sketch, "E266.MirrorCS", {"start": v(80.75, 72) * mm, "mid": v(80, 72.75) * mm, "end": v(79.25, 72) * mm});
            skArc(sketch, "E267.MirrorCS", {"start": v(79.25, 70.5) * mm, "mid": v(80, 69.75) * mm, "end": v(80.75, 70.5) * mm});
            skLineSegment(sketch, "E268.MirrorCS", {"start": v(79.25, 72) * mm, "end": v(79.25, 70.5) * mm});
            skLineSegment(sketch, "E269.MirrorCS", {"start": v(80.75, 72) * mm, "end": v(80.75, 70.5) * mm});
            skArc(sketch, "E270.MirrorCS", {"start": v(89.5, 79.25) * mm, "mid": v(90.25, 80) * mm, "end": v(89.5, 80.75) * mm});
            skArc(sketch, "E271.MirrorCS", {"start": v(88, 80.75) * mm, "mid": v(87.25, 80) * mm, "end": v(88, 79.25) * mm});
            skLineSegment(sketch, "E272.MirrorCS", {"start": v(88, 80.75) * mm, "end": v(89.5, 80.75) * mm});
            skLineSegment(sketch, "E273.MirrorCS", {"start": v(88, 79.25) * mm, "end": v(89.5, 79.25) * mm});
            skArc(sketch, "E274.MirrorCS", {"start": v(-80.75, -89.5) * mm, "mid": v(-80, -90.25) * mm, "end": v(-79.25, -89.5) * mm});
            skArc(sketch, "E275.MirrorCS", {"start": v(-79.25, -88) * mm, "mid": v(-80, -87.25) * mm, "end": v(-80.75, -88) * mm});
            skLineSegment(sketch, "E276.MirrorCS", {"start": v(-80.75, -88) * mm, "end": v(-80.75, -89.5) * mm});
            skArc(sketch, "E277.MirrorCS", {"start": v(-72, -79.25) * mm, "mid": v(-72.75, -80) * mm, "end": v(-72, -80.75) * mm});
            skLineSegment(sketch, "E278.MirrorCS", {"start": v(-72, -80.75) * mm, "end": v(-70.5, -80.75) * mm});
            skArc(sketch, "E279.MirrorCS", {"start": v(-70.5, -80.75) * mm, "mid": v(-69.75, -80) * mm, "end": v(-70.5, -79.25) * mm});
            skLineSegment(sketch, "E280.MirrorCS", {"start": v(-72, -79.25) * mm, "end": v(-70.5, -79.25) * mm});
            skArc(sketch, "E281.MirrorCS", {"start": v(-80.75, -72) * mm, "mid": v(-80, -72.75) * mm, "end": v(-79.25, -72) * mm});
            skLineSegment(sketch, "E282.MirrorCS", {"start": v(-80.75, -72) * mm, "end": v(-80.75, -70.5) * mm});
            skArc(sketch, "E283.MirrorCS", {"start": v(-79.25, -70.5) * mm, "mid": v(-80, -69.75) * mm, "end": v(-80.75, -70.5) * mm});
            skLineSegment(sketch, "E284.MirrorCS", {"start": v(-79.25, -72) * mm, "end": v(-79.25, -70.5) * mm});
            skArc(sketch, "E285.MirrorCS", {"start": v(-88, -80.75) * mm, "mid": v(-87.25, -80) * mm, "end": v(-88, -79.25) * mm});
            skLineSegment(sketch, "E286.MirrorCS", {"start": v(-88, -80.75) * mm, "end": v(-89.5, -80.75) * mm});
            skLineSegment(sketch, "E287.MirrorCS", {"start": v(-88, -79.25) * mm, "end": v(-89.5, -79.25) * mm});
            skArc(sketch, "E288.MirrorCS", {"start": v(-89.5, -79.25) * mm, "mid": v(-90.25, -80) * mm, "end": v(-89.5, -80.75) * mm});
            skArc(sketch, "E289.MirrorCS", {"start": v(79.25, -88) * mm, "mid": v(80, -87.25) * mm, "end": v(80.75, -88) * mm});
            skArc(sketch, "E290.MirrorCS", {"start": v(80.75, -89.5) * mm, "mid": v(80, -90.25) * mm, "end": v(79.25, -89.5) * mm});
            skLineSegment(sketch, "E291.MirrorCS", {"start": v(80.75, -88) * mm, "end": v(80.75, -89.5) * mm});
            skLineSegment(sketch, "E292.MirrorCS", {"start": v(79.25, -88) * mm, "end": v(79.25, -89.5) * mm});
            skArc(sketch, "E293.MirrorCS", {"start": v(89.5, -79.25) * mm, "mid": v(90.25, -80) * mm, "end": v(89.5, -80.75) * mm});
            skLineSegment(sketch, "E294.MirrorCS", {"start": v(88, -79.25) * mm, "end": v(89.5, -79.25) * mm});
            skArc(sketch, "E295.MirrorCS", {"start": v(88, -80.75) * mm, "mid": v(87.25, -80) * mm, "end": v(88, -79.25) * mm});
            skLineSegment(sketch, "E296.MirrorCS", {"start": v(88, -80.75) * mm, "end": v(89.5, -80.75) * mm});
            skLineSegment(sketch, "E297.MirrorCS", {"start": v(79.25, -72) * mm, "end": v(79.25, -70.5) * mm});
            skLineSegment(sketch, "E298.MirrorCS", {"start": v(80.75, -72) * mm, "end": v(80.75, -70.5) * mm});
            skArc(sketch, "E299.MirrorCS", {"start": v(80.75, -72) * mm, "mid": v(80, -72.75) * mm, "end": v(79.25, -72) * mm});
            skArc(sketch, "E300.MirrorCS", {"start": v(79.25, -70.5) * mm, "mid": v(80, -69.75) * mm, "end": v(80.75, -70.5) * mm});
            skArc(sketch, "E301.MirrorCS", {"start": v(72, -79.25) * mm, "mid": v(72.75, -80) * mm, "end": v(72, -80.75) * mm});
            skArc(sketch, "E302.MirrorCS", {"start": v(70.5, -80.75) * mm, "mid": v(69.75, -80) * mm, "end": v(70.5, -79.25) * mm});
            skLineSegment(sketch, "E303.MirrorCS", {"start": v(72, -80.75) * mm, "end": v(70.5, -80.75) * mm});
            skLineSegment(sketch, "E304.MirrorCS", {"start": v(72, -79.25) * mm, "end": v(70.5, -79.25) * mm});
            skLineSegment(sketch, "E305", {"start": v(-79.25, -88) * mm, "end": v(-79.25, -89.5) * mm});
            skSolve(sketch);
        }
        {
            var Q0;
            Q0=makeQuery(id+"F0.imprint","IMPRINT",FACE,{"disambiguationData":[TD([[makeQuery(id+"F0.imprint","IMPRINT",EDGE,{"derivedFrom":sQuery(id+"F0.wireOp",EDGE,"E1")}),1.0]])]});
            var Q1;
            Q1=makeQuery(id+"F0.imprint","IMPRINT",FACE,{"disambiguationData":[TD([[makeQuery(id+"F0.imprint","IMPRINT",EDGE,{"derivedFrom":sQuery(id+"F0.wireOp",EDGE,"E10.rect.bottom")}),-1.0]])]});
            extrude(context, id + "F1", {"entities" : qUnion([Q0, Q1]), "depth" : 2 * mm});
        }
        {
            var Q0;
            Q0=makeQuery(id+"F1.opExtrude","CAP_FACE",FACE,{"disambiguationData":[OSD([sQuery(id+"F0.wireOp",EDGE,"E1"),sQuery(id+"F0.wireOp",EDGE,"E2"),sQuery(id+"F0.wireOp",EDGE,"E4"),sQuery(id+"F0.wireOp",EDGE,"E11.0"),sQuery(id+"F0.wireOp",EDGE,"E11.1"),sQuery(id+"F0.wireOp",EDGE,"E11.2"),sQuery(id+"F0.wireOp",EDGE,"E11.3"),sQuery(id+"F0.wireOp",EDGE,"E12.0"),sQuery(id+"F0.wireOp",EDGE,"E12.1"),sQuery(id+"F0.wireOp",EDGE,"E12.2"),sQuery(id+"F0.wireOp",EDGE,"E12.3"),sQuery(id+"F0.wireOp",EDGE,"E13"),sQuery(id+"F0.wireOp",EDGE,"E14"),sQuery(id+"F0.wireOp",EDGE,"E15"),sQuery(id+"F0.wireOp",EDGE,"E16"),sQuery(id+"F0.wireOp",EDGE,"E17.trimOffspring"),sQuery(id+"F0.wireOp",EDGE,"E20.trimOffspring"),sQuery(id+"F0.wireOp",EDGE,"E21.trimOffspring"),sQuery(id+"F0.wireOp",EDGE,"E22.trimOffspring"),sQuery(id+"F0.wireOp",EDGE,"E23.trimOffspring"),sQuery(id+"F0.wireOp",EDGE,"E28.0"),sQuery(id+"F0.wireOp",EDGE,"E29.0"),sQuery(id+"F0.wireOp",EDGE,"E30.0"),sQuery(id+"F0.wireOp",EDGE,"E31.0"),sQuery(id+"F0.wireOp",EDGE,"E32.0"),sQuery(id+"F0.wireOp",EDGE,"E33.0"),sQuery(id+"F0.wireOp",EDGE,"E34.0"),sQuery(id+"F0.wireOp",EDGE,"E35.0"),sQuery(id+"F0.wireOp",EDGE,"E52.trimOffspring"),sQuery(id+"F0.wireOp",EDGE,"E53.filletArc"),sQuery(id+"F0.wireOp",EDGE,"E54.trimOffspring"),sQuery(id+"F0.wireOp",EDGE,"E55.trimOffspring"),sQuery(id+"F0.wireOp",EDGE,"E56.trimOffspring"),sQuery(id+"F0.wireOp",EDGE,"E57.filletArc"),sQuery(id+"F0.wireOp",EDGE,"E58.filletArc"),sQuery(id+"F0.wireOp",EDGE,"E59.filletArc"),sQuery(id+"F0.wireOp",EDGE,"E60.filletArc"),sQuery(id+"F0.wireOp",EDGE,"E61.filletArc"),sQuery(id+"F0.wireOp",EDGE,"E62.filletArc"),sQuery(id+"F0.wireOp",EDGE,"E63.filletArc"),sQuery(id+"F0.wireOp",EDGE,"E66.filletArc"),sQuery(id+"F0.wireOp",EDGE,"E67.filletArc"),sQuery(id+"F0.wireOp",EDGE,"E68.filletArc"),sQuery(id+"F0.wireOp",EDGE,"E69.filletArc"),sQuery(id+"F0.wireOp",EDGE,"E70.filletArc"),sQuery(id+"F0.wireOp",EDGE,"E71.filletArc"),sQuery(id+"F0.wireOp",EDGE,"E72.filletArc"),sQuery(id+"F0.wireOp",EDGE,"E73.filletArc"),sQuery(id+"F0.wireOp",EDGE,"E74.filletArc"),sQuery(id+"F0.wireOp",EDGE,"E75.filletArc"),sQuery(id+"F0.wireOp",EDGE,"E76.filletArc"),sQuery(id+"F0.wireOp",EDGE,"E77.filletArc"),sQuery(id+"F0.wireOp",EDGE,"E78.filletArc"),sQuery(id+"F0.wireOp",EDGE,"E79.filletArc"),sQuery(id+"F0.wireOp",EDGE,"E80.filletArc"),sQuery(id+"F0.wireOp",EDGE,"E81.filletArc"),sQuery(id+"F0.wireOp",EDGE,"E83.filletArc"),sQuery(id+"F0.wireOp",EDGE,"E84.filletArc"),sQuery(id+"F0.wireOp",EDGE,"E85.filletArc"),sQuery(id+"F0.wireOp",EDGE,"E86.filletArc"),sQuery(id+"F0.wireOp",EDGE,"E87.filletArc"),sQuery(id+"F0.wireOp",EDGE,"E88.filletArc"),sQuery(id+"F0.wireOp",EDGE,"E89.filletArc"),sQuery(id+"F0.wireOp",EDGE,"E90.filletArc"),sQuery(id+"F0.wireOp",EDGE,"E91"),sQuery(id+"F0.wireOp",EDGE,"E13"),sQuery(id+"F0.wireOp",EDGE,"E16"),sQuery(id+"F0.wireOp",EDGE,"E92.trimOffspring"),sQuery(id+"F0.wireOp",EDGE,"E93.trimOffspring"),sQuery(id+"F0.wireOp",EDGE,"E94.trimOffspring"),sQuery(id+"F0.wireOp",EDGE,"E95.trimOffspring"),sQuery(id+"F0.wireOp",EDGE,"E96.trimOffspring"),sQuery(id+"F0.wireOp",EDGE,"E97.filletArc"),sQuery(id+"F0.wireOp",EDGE,"E98.filletArc"),sQuery(id+"F0.wireOp",EDGE,"E99.filletArc"),sQuery(id+"F0.wireOp",EDGE,"E100.filletArc"),sQuery(id+"F0.wireOp",EDGE,"E101.filletArc"),sQuery(id+"F0.wireOp",EDGE,"E102.filletArc"),sQuery(id+"F0.wireOp",EDGE,"E103.filletArc"),sQuery(id+"F0.wireOp",EDGE,"E104.filletArc"),sQuery(id+"F0.wireOp",EDGE,"E105"),sQuery(id+"F0.wireOp",EDGE,"E106"),sQuery(id+"F0.wireOp",EDGE,"E107"),sQuery(id+"F0.wireOp",EDGE,"E108"),sQuery(id+"F0.wireOp",EDGE,"E109"),sQuery(id+"F0.wireOp",EDGE,"E113.MirrorC"),sQuery(id+"F0.wireOp",EDGE,"E110"),sQuery(id+"F0.wireOp",EDGE,"E114.MirrorC"),sQuery(id+"F0.wireOp",EDGE,"E115.filletArc"),sQuery(id+"F0.wireOp",EDGE,"E116.filletArc"),sQuery(id+"F0.wireOp",EDGE,"E117.filletArc"),sQuery(id+"F0.wireOp",EDGE,"E118.filletArc"),sQuery(id+"F0.wireOp",EDGE,"E119.filletArc"),sQuery(id+"F0.wireOp",EDGE,"E120.filletArc"),sQuery(id+"F0.wireOp",EDGE,"E121.filletArc"),sQuery(id+"F0.wireOp",EDGE,"E122.filletArc"),sQuery(id+"F0.wireOp",EDGE,"E123.filletArc"),sQuery(id+"F0.wireOp",EDGE,"E124.filletArc"),sQuery(id+"F0.wireOp",EDGE,"E125.filletArc"),sQuery(id+"F0.wireOp",EDGE,"E126.filletArc"),sQuery(id+"F0.wireOp",EDGE,"E127"),sQuery(id+"F0.wireOp",EDGE,"E128"),sQuery(id+"F0.wireOp",EDGE,"E129"),sQuery(id+"F0.wireOp",EDGE,"E134"),sQuery(id+"F0.wireOp",EDGE,"E135"),sQuery(id+"F0.wireOp",EDGE,"E136.trimOffspring"),sQuery(id+"F0.wireOp",EDGE,"E137.trimOffspring"),sQuery(id+"F0.wireOp",EDGE,"E138.trimOffspring"),sQuery(id+"F0.wireOp",EDGE,"E139.filletArc"),sQuery(id+"F0.wireOp",EDGE,"E140.filletArc"),sQuery(id+"F0.wireOp",EDGE,"E141.filletArc"),sQuery(id+"F0.wireOp",EDGE,"E142.filletArc"),sQuery(id+"F0.wireOp",EDGE,"E143.trimOffspring"),sQuery(id+"F0.wireOp",EDGE,"E144.trimOffspring"),sQuery(id+"F0.wireOp",EDGE,"E145.trimOffspring"),sQuery(id+"F0.wireOp",EDGE,"E146.filletArc"),sQuery(id+"F0.wireOp",EDGE,"E147.filletArc"),sQuery(id+"F0.wireOp",EDGE,"E148.filletArc"),sQuery(id+"F0.wireOp",EDGE,"E149.filletArc"),sQuery(id+"F0.wireOp",EDGE,"E150"),sQuery(id+"F0.wireOp",EDGE,"E151"),sQuery(id+"F0.wireOp",EDGE,"E152"),sQuery(id+"F0.wireOp",EDGE,"E153"),sQuery(id+"F0.wireOp",EDGE,"E154"),sQuery(id+"F0.wireOp",EDGE,"E155"),sQuery(id+"F0.wireOp",EDGE,"E156"),sQuery(id+"F0.wireOp",EDGE,"E157"),sQuery(id+"F0.wireOp",EDGE,"E158"),sQuery(id+"F0.wireOp",EDGE,"E159"),sQuery(id+"F0.wireOp",EDGE,"E160"),sQuery(id+"F0.wireOp",EDGE,"E161.MirrorCS"),sQuery(id+"F0.wireOp",EDGE,"E162.MirrorCS"),sQuery(id+"F0.wireOp",EDGE,"E163.MirrorC"),sQuery(id+"F0.wireOp",EDGE,"E164.MirrorCS"),sQuery(id+"F0.wireOp",EDGE,"E165.MirrorCS"),sQuery(id+"F0.wireOp",EDGE,"E166.MirrorCS"),sQuery(id+"F0.wireOp",EDGE,"E167.MirrorCS"),sQuery(id+"F0.wireOp",EDGE,"E168.MirrorC"),sQuery(id+"F0.wireOp",EDGE,"E169.MirrorCS"),sQuery(id+"F0.wireOp",EDGE,"E170.MirrorCS"),sQuery(id+"F0.wireOp",EDGE,"E171.MirrorCS"),sQuery(id+"F0.wireOp",EDGE,"E172.MirrorCS"),sQuery(id+"F0.wireOp",EDGE,"E173.MirrorCS"),sQuery(id+"F0.wireOp",EDGE,"E174.MirrorCS"),sQuery(id+"F0.wireOp",EDGE,"E176"),sQuery(id+"F0.wireOp",EDGE,"E177"),sQuery(id+"F0.wireOp",EDGE,"E178.trimOffspring"),sQuery(id+"F0.wireOp",EDGE,"E179.filletArc"),sQuery(id+"F0.wireOp",EDGE,"E180.filletArc"),sQuery(id+"F0.wireOp",EDGE,"E181.MirrorC"),sQuery(id+"F0.wireOp",EDGE,"E182.MirrorCS"),sQuery(id+"F0.wireOp",EDGE,"E183.MirrorCS"),sQuery(id+"F0.wireOp",EDGE,"E184.MirrorCS"),sQuery(id+"F0.wireOp",EDGE,"E185.trimOffspring"),sQuery(id+"F0.wireOp",EDGE,"E186.trimOffspring"),sQuery(id+"F0.wireOp",EDGE,"E187.trimOffspring"),sQuery(id+"F0.wireOp",EDGE,"E188.trimOffspring"),sQuery(id+"F0.wireOp",EDGE,"E189.trimOffspring"),sQuery(id+"F0.wireOp",EDGE,"E190.MirrorCS"),sQuery(id+"F0.wireOp",EDGE,"E191.MirrorCS"),sQuery(id+"F0.wireOp",EDGE,"E192.MirrorCS"),sQuery(id+"F0.wireOp",EDGE,"E193.MirrorCS"),sQuery(id+"F0.wireOp",EDGE,"E194.MirrorCS"),sQuery(id+"F0.wireOp",EDGE,"E195.MirrorCS"),sQuery(id+"F0.wireOp",EDGE,"E196.MirrorCS"),sQuery(id+"F0.wireOp",EDGE,"E197.MirrorCS"),sQuery(id+"F0.wireOp",EDGE,"E198.MirrorCS"),sQuery(id+"F0.wireOp",EDGE,"E199.MirrorCS"),sQuery(id+"F0.wireOp",EDGE,"E200.MirrorCS"),sQuery(id+"F0.wireOp",EDGE,"E201.MirrorCS"),sQuery(id+"F0.wireOp",EDGE,"E202.MirrorCS"),sQuery(id+"F0.wireOp",EDGE,"E203.MirrorCS"),sQuery(id+"F0.wireOp",EDGE,"E204.MirrorCS"),sQuery(id+"F0.wireOp",EDGE,"E205.MirrorCS"),sQuery(id+"F0.wireOp",EDGE,"E206.MirrorCS"),sQuery(id+"F0.wireOp",EDGE,"E207.MirrorCS"),sQuery(id+"F0.wireOp",EDGE,"E208.MirrorCS"),sQuery(id+"F0.wireOp",EDGE,"E209.MirrorCS"),sQuery(id+"F0.wireOp",EDGE,"E210.MirrorC"),sQuery(id+"F0.wireOp",EDGE,"E211.MirrorC"),sQuery(id+"F0.wireOp",EDGE,"E212.MirrorC"),sQuery(id+"F0.wireOp",EDGE,"E213.MirrorC"),sQuery(id+"F0.wireOp",EDGE,"E214.MirrorC"),sQuery(id+"F0.wireOp",EDGE,"E215.MirrorCS"),sQuery(id+"F0.wireOp",EDGE,"E216.MirrorCS"),sQuery(id+"F0.wireOp",EDGE,"E217.MirrorCS"),sQuery(id+"F0.wireOp",EDGE,"E218.MirrorCS"),sQuery(id+"F0.wireOp",EDGE,"E219.MirrorCS"),sQuery(id+"F0.wireOp",EDGE,"E220.MirrorCS"),sQuery(id+"F0.wireOp",EDGE,"E221.MirrorC"),sQuery(id+"F0.wireOp",EDGE,"E222.MirrorCS"),sQuery(id+"F0.wireOp",EDGE,"E223.MirrorCS"),sQuery(id+"F0.wireOp",EDGE,"E224.MirrorCS"),sQuery(id+"F0.wireOp",EDGE,"E225.trimOffspring"),sQuery(id+"F0.wireOp",EDGE,"E226.trimOffspring"),sQuery(id+"F0.wireOp",EDGE,"E227.trimOffspring"),sQuery(id+"F0.wireOp",EDGE,"E228.trimOffspring"),sQuery(id+"F0.wireOp",EDGE,"E229.trimOffspring"),sQuery(id+"F0.wireOp",EDGE,"E230.trimOffspring"),sQuery(id+"F0.wireOp",EDGE,"E231.MirrorCS"),sQuery(id+"F0.wireOp",EDGE,"E232.trimOffspring"),sQuery(id+"F0.wireOp",EDGE,"E233.trimOffspring"),sQuery(id+"F0.wireOp",EDGE,"E234.trimOffspring"),sQuery(id+"F0.wireOp",EDGE,"E235.trimOffspring"),sQuery(id+"F0.wireOp",EDGE,"E239"),sQuery(id+"F0.wireOp",EDGE,"E241"),sQuery(id+"F0.wireOp",EDGE,"E242.MirrorC"),sQuery(id+"F0.wireOp",EDGE,"E243.MirrorC"),sQuery(id+"F0.wireOp",EDGE,"E245"),sQuery(id+"F0.wireOp",EDGE,"E246"),sQuery(id+"F0.wireOp",EDGE,"E247"),sQuery(id+"F0.wireOp",EDGE,"E248"),sQuery(id+"F0.wireOp",EDGE,"E255.0.startCap"),sQuery(id+"F0.wireOp",EDGE,"E255.0.endCap"),sQuery(id+"F0.wireOp",EDGE,"E255.0.left"),sQuery(id+"F0.wireOp",EDGE,"E255.0.right"),sQuery(id+"F0.wireOp",EDGE,"E256.0.startCap"),sQuery(id+"F0.wireOp",EDGE,"E256.0.endCap"),sQuery(id+"F0.wireOp",EDGE,"E256.0.left"),sQuery(id+"F0.wireOp",EDGE,"E256.0.right"),sQuery(id+"F0.wireOp",EDGE,"E257.0.startCap"),sQuery(id+"F0.wireOp",EDGE,"E257.0.endCap"),sQuery(id+"F0.wireOp",EDGE,"E257.0.left"),sQuery(id+"F0.wireOp",EDGE,"E257.0.right"),sQuery(id+"F0.wireOp",EDGE,"E257.1.startCap"),sQuery(id+"F0.wireOp",EDGE,"E257.1.endCap"),sQuery(id+"F0.wireOp",EDGE,"E257.1.left"),sQuery(id+"F0.wireOp",EDGE,"E257.1.right"),sQuery(id+"F0.wireOp",EDGE,"E258.MirrorCS"),sQuery(id+"F0.wireOp",EDGE,"E259.MirrorCS"),sQuery(id+"F0.wireOp",EDGE,"E260.MirrorCS"),sQuery(id+"F0.wireOp",EDGE,"E261.MirrorCS"),sQuery(id+"F0.wireOp",EDGE,"E262.MirrorCS"),sQuery(id+"F0.wireOp",EDGE,"E263.MirrorCS"),sQuery(id+"F0.wireOp",EDGE,"E264.MirrorCS"),sQuery(id+"F0.wireOp",EDGE,"E265.MirrorCS"),sQuery(id+"F0.wireOp",EDGE,"E266.MirrorCS"),sQuery(id+"F0.wireOp",EDGE,"E267.MirrorCS"),sQuery(id+"F0.wireOp",EDGE,"E268.MirrorCS"),sQuery(id+"F0.wireOp",EDGE,"E269.MirrorCS"),sQuery(id+"F0.wireOp",EDGE,"E270.MirrorCS"),sQuery(id+"F0.wireOp",EDGE,"E271.MirrorCS"),sQuery(id+"F0.wireOp",EDGE,"E272.MirrorCS"),sQuery(id+"F0.wireOp",EDGE,"E273.MirrorCS"),sQuery(id+"F0.wireOp",EDGE,"E274.MirrorCS"),sQuery(id+"F0.wireOp",EDGE,"E275.MirrorCS"),sQuery(id+"F0.wireOp",EDGE,"E276.MirrorCS"),sQuery(id+"F0.wireOp",EDGE,"E277.MirrorCS"),sQuery(id+"F0.wireOp",EDGE,"E278.MirrorCS"),sQuery(id+"F0.wireOp",EDGE,"E279.MirrorCS"),sQuery(id+"F0.wireOp",EDGE,"E280.MirrorCS"),sQuery(id+"F0.wireOp",EDGE,"E281.MirrorCS"),sQuery(id+"F0.wireOp",EDGE,"E282.MirrorCS"),sQuery(id+"F0.wireOp",EDGE,"E283.MirrorCS"),sQuery(id+"F0.wireOp",EDGE,"E284.MirrorCS"),sQuery(id+"F0.wireOp",EDGE,"E285.MirrorCS"),sQuery(id+"F0.wireOp",EDGE,"E286.MirrorCS"),sQuery(id+"F0.wireOp",EDGE,"E287.MirrorCS"),sQuery(id+"F0.wireOp",EDGE,"E288.MirrorCS"),sQuery(id+"F0.wireOp",EDGE,"E289.MirrorCS"),sQuery(id+"F0.wireOp",EDGE,"E290.MirrorCS"),sQuery(id+"F0.wireOp",EDGE,"E291.MirrorCS"),sQuery(id+"F0.wireOp",EDGE,"E292.MirrorCS"),sQuery(id+"F0.wireOp",EDGE,"E293.MirrorCS"),sQuery(id+"F0.wireOp",EDGE,"E294.MirrorCS"),sQuery(id+"F0.wireOp",EDGE,"E295.MirrorCS"),sQuery(id+"F0.wireOp",EDGE,"E296.MirrorCS"),sQuery(id+"F0.wireOp",EDGE,"E297.MirrorCS"),sQuery(id+"F0.wireOp",EDGE,"E298.MirrorCS"),sQuery(id+"F0.wireOp",EDGE,"E299.MirrorCS"),sQuery(id+"F0.wireOp",EDGE,"E300.MirrorCS"),sQuery(id+"F0.wireOp",EDGE,"E301.MirrorCS"),sQuery(id+"F0.wireOp",EDGE,"E302.MirrorCS"),sQuery(id+"F0.wireOp",EDGE,"E303.MirrorCS"),sQuery(id+"F0.wireOp",EDGE,"E304.MirrorCS"),sQuery(id+"F0.wireOp",EDGE,"E305")])],"isStart":true});
            var sketch = newSketch(context, id + "F2", { "sketchPlane" : qUnion([Q0])});
            skLineSegment(sketch, "E306.rect.bottom", {"start": v(20, -51) * mm, "end": v(-20, -51) * mm});
            skLineSegment(sketch, "E306.rect.left", {"start": v(25, -46) * mm, "end": v(25, 0) * mm});
            skLineSegment(sketch, "E306.rect.right", {"start": v(-25, -46) * mm, "end": v(-25, 0) * mm});
            skPoint(sketch, "E306.rect.middle", {"position": v(0, 0) * mm});
            skPoint(sketch, "E307.visualSharp", {"position": v(-25, 51) * mm});
            skPoint(sketch, "E308.visualSharp", {"position": v(25, 51) * mm});
            skPoint(sketch, "E309.visualSharp", {"position": v(25, -51) * mm});
            skArc(sketch, "E309.filletArc", {"start": v(20, -51) * mm, "mid": v(23.54, -49.54) * mm, "end": v(25, -46) * mm});
            skPoint(sketch, "E310.visualSharp", {"position": v(-25, -51) * mm});
            skArc(sketch, "E310.filletArc", {"start": v(-25, -46) * mm, "mid": v(-23.54, -49.54) * mm, "end": v(-20, -51) * mm});
            skLineSegment(sketch, "E311.rect.bottom", {"start": v(21.5, -27.47) * mm, "end": v(-21.5, -27.47) * mm, "construction": true});
            skLineSegment(sketch, "E311.rect.top", {"start": v(21.5, 27.47) * mm, "end": v(-21.5, 27.47) * mm, "construction": true});
            skLineSegment(sketch, "E311.rect.left", {"start": v(21.5, -27.47) * mm, "end": v(21.5, 27.47) * mm, "construction": true});
            skLineSegment(sketch, "E311.rect.right", {"start": v(-21.5, -27.47) * mm, "end": v(-21.5, 27.47) * mm, "construction": true});
            skLineSegment(sketch, "E312.rect.bottom", {"start": v(14.03, -51) * mm, "end": v(-14.03, -51) * mm, "construction": true});
            skLineSegment(sketch, "E312.rect.top", {"start": v(14.03, 51) * mm, "end": v(-14.03, 51) * mm, "construction": true});
            skLineSegment(sketch, "E312.rect.left", {"start": v(14.03, -51) * mm, "end": v(14.03, 51) * mm, "construction": true});
            skLineSegment(sketch, "E312.rect.right", {"start": v(-14.03, -51) * mm, "end": v(-14.03, 51) * mm, "construction": true});
            skLineSegment(sketch, "E313", {"start": v(-14.03, 0) * mm, "end": v(14.03, 0) * mm});
            skArc(sketch, "E314.0.startCap", {"start": v(-14.03, -2) * mm, "mid": v(-16.03, 0) * mm, "end": v(-14.03, 2) * mm});
            skArc(sketch, "E314.0.endCap", {"start": v(14.03, 2) * mm, "mid": v(16.03, 0) * mm, "end": v(14.03, -2) * mm});
            skLineSegment(sketch, "E314.0.left", {"start": v(-14.03, 2) * mm, "end": v(14.03, 2) * mm});
            skLineSegment(sketch, "E314.0.right", {"start": v(-14.03, -2) * mm, "end": v(14.03, -2) * mm});
            skLineSegment(sketch, "E315.direction1", {"start": v(0, 0) * mm, "end": v(25, 0) * mm, "construction": true});
            skLineSegment(sketch, "E315.direction2", {"start": v(0, 0) * mm, "end": v(0, 7.2) * mm, "construction": true});
            skLineSegment(sketch, "E316.rect.bottom", {"start": v(-21.5, -15) * mm, "end": v(-21.5, -15) * mm});
            skLineSegment(sketch, "E316.rect.top", {"start": v(-21.5, 15) * mm, "end": v(-21.5, 15) * mm});
            skLineSegment(sketch, "E316.rect.left", {"start": v(-21.5, -15) * mm, "end": v(-21.5, 15) * mm});
            skLineSegment(sketch, "E316.rect.right", {"start": v(-21.5, -15) * mm, "end": v(-21.5, 15) * mm});
            skPoint(sketch, "E316.rect.middle", {"position": v(-21.5, 0) * mm});
            skLineSegment(sketch, "E317.MirrorCS", {"start": v(21.5, -15) * mm, "end": v(21.5, 15) * mm});
            skArc(sketch, "E318.0.startCap", {"start": v(-20, -15) * mm, "mid": v(-21.5, -16.5) * mm, "end": v(-23, -15) * mm});
            skArc(sketch, "E318.0.endCap", {"start": v(-23, 15) * mm, "mid": v(-21.5, 16.5) * mm, "end": v(-20, 15) * mm});
            skLineSegment(sketch, "E318.0.left", {"start": v(-23, -15) * mm, "end": v(-23, 15) * mm});
            skLineSegment(sketch, "E318.0.right", {"start": v(-20, -15) * mm, "end": v(-20, 15) * mm});
            skArc(sketch, "E319.0.startCap", {"start": v(23, -15) * mm, "mid": v(21.5, -16.5) * mm, "end": v(20, -15) * mm});
            skArc(sketch, "E319.0.endCap", {"start": v(20, 15) * mm, "mid": v(21.5, 16.5) * mm, "end": v(23, 15) * mm});
            skLineSegment(sketch, "E319.0.left", {"start": v(20, -15) * mm, "end": v(20, 15) * mm});
            skLineSegment(sketch, "E319.0.right", {"start": v(23, -15) * mm, "end": v(23, 15) * mm});
            skLineSegment(sketch, "E320", {"start": v(25, 0) * mm, "end": v(25, 46) * mm});
            skLineSegment(sketch, "E321", {"start": v(-25, 0) * mm, "end": v(-25, 46) * mm});
            skLineSegment(sketch, "E322.top", {"start": v(-20, 60) * mm, "end": v(20, 60) * mm});
            skLineSegment(sketch, "E322.left", {"start": v(-25, 46) * mm, "end": v(-25, 55) * mm});
            skLineSegment(sketch, "E322.right", {"start": v(25, 46) * mm, "end": v(25, 55) * mm});
            skPoint(sketch, "E323.visualSharp", {"position": v(-25, 60) * mm});
            skArc(sketch, "E323.filletArc", {"start": v(-20, 60) * mm, "mid": v(-23.54, 58.54) * mm, "end": v(-25, 55) * mm});
            skPoint(sketch, "E324.visualSharp", {"position": v(25, 60) * mm});
            skArc(sketch, "E324.filletArc", {"start": v(25, 55) * mm, "mid": v(23.54, 58.54) * mm, "end": v(20, 60) * mm});
            skPoint(sketch, "E325.0.1.0", {"position": v(0, 7.4) * mm});
            skLineSegment(sketch, "E325.0.1.1", {"start": v(-14.03, 9.4) * mm, "end": v(14.03, 9.4) * mm});
            skLineSegment(sketch, "E325.0.1.2", {"start": v(-14.03, 5.4) * mm, "end": v(14.03, 5.4) * mm});
            skLineSegment(sketch, "E325.0.1.3", {"start": v(-14.03, 7.4) * mm, "end": v(14.03, 7.4) * mm});
            skArc(sketch, "E325.0.1.4", {"start": v(14.03, 9.4) * mm, "mid": v(16.03, 7.4) * mm, "end": v(14.03, 5.4) * mm});
            skPoint(sketch, "E325.0.1.5", {"position": v(0, 7.4) * mm});
            skArc(sketch, "E325.0.1.6", {"start": v(-14.03, 5.4) * mm, "mid": v(-16.03, 7.4) * mm, "end": v(-14.03, 9.4) * mm});
            skPoint(sketch, "E325.0.1.7", {"position": v(0, 7.4) * mm});
            skPoint(sketch, "E325.0.2.0", {"position": v(0, 14.8) * mm});
            skLineSegment(sketch, "E325.0.2.1", {"start": v(-14.03, 16.8) * mm, "end": v(14.03, 16.8) * mm});
            skLineSegment(sketch, "E325.0.2.2", {"start": v(-14.03, 12.8) * mm, "end": v(14.03, 12.8) * mm});
            skLineSegment(sketch, "E325.0.2.3", {"start": v(-14.03, 14.8) * mm, "end": v(14.03, 14.8) * mm});
            skArc(sketch, "E325.0.2.4", {"start": v(14.03, 16.8) * mm, "mid": v(16.03, 14.8) * mm, "end": v(14.03, 12.8) * mm});
            skPoint(sketch, "E325.0.2.5", {"position": v(0, 14.8) * mm});
            skArc(sketch, "E325.0.2.6", {"start": v(-14.03, 12.8) * mm, "mid": v(-16.03, 14.8) * mm, "end": v(-14.03, 16.8) * mm});
            skPoint(sketch, "E325.0.2.7", {"position": v(0, 14.8) * mm});
            skPoint(sketch, "E325.0.3.0", {"position": v(0, 22.2) * mm});
            skLineSegment(sketch, "E325.0.3.1", {"start": v(-14.03, 24.2) * mm, "end": v(14.03, 24.2) * mm});
            skLineSegment(sketch, "E325.0.3.2", {"start": v(-14.03, 20.2) * mm, "end": v(14.03, 20.2) * mm});
            skLineSegment(sketch, "E325.0.3.3", {"start": v(-14.03, 22.2) * mm, "end": v(14.03, 22.2) * mm});
            skArc(sketch, "E325.0.3.4", {"start": v(14.03, 24.2) * mm, "mid": v(16.03, 22.2) * mm, "end": v(14.03, 20.2) * mm});
            skPoint(sketch, "E325.0.3.5", {"position": v(0, 22.2) * mm});
            skArc(sketch, "E325.0.3.6", {"start": v(-14.03, 20.2) * mm, "mid": v(-16.03, 22.2) * mm, "end": v(-14.03, 24.2) * mm});
            skPoint(sketch, "E325.0.3.7", {"position": v(0, 22.2) * mm});
            skPoint(sketch, "E325.0.4.0", {"position": v(0, 29.6) * mm});
            skLineSegment(sketch, "E325.0.4.1", {"start": v(-14.03, 31.6) * mm, "end": v(14.03, 31.6) * mm});
            skLineSegment(sketch, "E325.0.4.2", {"start": v(-14.03, 27.6) * mm, "end": v(14.03, 27.6) * mm});
            skLineSegment(sketch, "E325.0.4.3", {"start": v(-14.03, 29.6) * mm, "end": v(14.03, 29.6) * mm});
            skArc(sketch, "E325.0.4.4", {"start": v(14.03, 31.6) * mm, "mid": v(16.03, 29.6) * mm, "end": v(14.03, 27.6) * mm});
            skPoint(sketch, "E325.0.4.5", {"position": v(0, 29.6) * mm});
            skArc(sketch, "E325.0.4.6", {"start": v(-14.03, 27.6) * mm, "mid": v(-16.03, 29.6) * mm, "end": v(-14.03, 31.6) * mm});
            skPoint(sketch, "E325.0.4.7", {"position": v(0, 29.6) * mm});
            skPoint(sketch, "E325.0.5.0", {"position": v(0, 37) * mm});
            skLineSegment(sketch, "E325.0.5.1", {"start": v(-14.03, 39) * mm, "end": v(14.03, 39) * mm});
            skLineSegment(sketch, "E325.0.5.2", {"start": v(-14.03, 35) * mm, "end": v(14.03, 35) * mm});
            skLineSegment(sketch, "E325.0.5.3", {"start": v(-14.03, 37) * mm, "end": v(14.03, 37) * mm});
            skArc(sketch, "E325.0.5.4", {"start": v(14.03, 39) * mm, "mid": v(16.03, 37) * mm, "end": v(14.03, 35) * mm});
            skPoint(sketch, "E325.0.5.5", {"position": v(0, 37) * mm});
            skArc(sketch, "E325.0.5.6", {"start": v(-14.03, 35) * mm, "mid": v(-16.03, 37) * mm, "end": v(-14.03, 39) * mm});
            skPoint(sketch, "E325.0.5.7", {"position": v(0, 37) * mm});
            skPoint(sketch, "E325.0.6.0", {"position": v(0, 44.4) * mm});
            skLineSegment(sketch, "E325.0.6.1", {"start": v(-14.03, 46.4) * mm, "end": v(14.03, 46.4) * mm});
            skLineSegment(sketch, "E325.0.6.2", {"start": v(-14.03, 42.4) * mm, "end": v(14.03, 42.4) * mm});
            skLineSegment(sketch, "E325.0.6.3", {"start": v(-14.03, 44.4) * mm, "end": v(14.03, 44.4) * mm});
            skArc(sketch, "E325.0.6.4", {"start": v(14.03, 46.4) * mm, "mid": v(16.03, 44.4) * mm, "end": v(14.03, 42.4) * mm});
            skPoint(sketch, "E325.0.6.5", {"position": v(0, 44.4) * mm});
            skArc(sketch, "E325.0.6.6", {"start": v(-14.03, 42.4) * mm, "mid": v(-16.03, 44.4) * mm, "end": v(-14.03, 46.4) * mm});
            skPoint(sketch, "E325.0.6.7", {"position": v(0, 44.4) * mm});
            skPoint(sketch, "E325.0.7.0", {"position": v(0, 51.8) * mm});
            skLineSegment(sketch, "E325.0.7.1", {"start": v(-14.03, 53.8) * mm, "end": v(14.03, 53.8) * mm});
            skLineSegment(sketch, "E325.0.7.2", {"start": v(-14.03, 49.8) * mm, "end": v(14.03, 49.8) * mm});
            skLineSegment(sketch, "E325.0.7.3", {"start": v(-14.03, 51.8) * mm, "end": v(14.03, 51.8) * mm});
            skArc(sketch, "E325.0.7.4", {"start": v(14.03, 53.8) * mm, "mid": v(16.03, 51.8) * mm, "end": v(14.03, 49.8) * mm});
            skPoint(sketch, "E325.0.7.5", {"position": v(0, 51.8) * mm});
            skArc(sketch, "E325.0.7.6", {"start": v(-14.03, 49.8) * mm, "mid": v(-16.03, 51.8) * mm, "end": v(-14.03, 53.8) * mm});
            skPoint(sketch, "E325.0.7.7", {"position": v(0, 51.8) * mm});
            skLineSegment(sketch, "E325.direction2", {"start": v(0, 0) * mm, "end": v(0, 7.4) * mm, "construction": true});
            skPoint(sketch, "E326.MirrorP", {"position": v(0, -37) * mm});
            skPoint(sketch, "E327.MirrorP", {"position": v(0, -22.2) * mm});
            skPoint(sketch, "E328.MirrorP", {"position": v(0, -7.4) * mm});
            skPoint(sketch, "E329.MirrorP", {"position": v(0, -29.6) * mm});
            skArc(sketch, "E330.MirrorCS", {"start": v(14.03, -39) * mm, "mid": v(16.03, -37) * mm, "end": v(14.03, -35) * mm});
            skArc(sketch, "E331.MirrorCS", {"start": v(-14.03, -35) * mm, "mid": v(-16.03, -37) * mm, "end": v(-14.03, -39) * mm});
            skPoint(sketch, "E332.MirrorP", {"position": v(0, -14.8) * mm});
            skArc(sketch, "E333.MirrorCS", {"start": v(-14.03, -20.2) * mm, "mid": v(-16.03, -22.2) * mm, "end": v(-14.03, -24.2) * mm});
            skArc(sketch, "E334.MirrorCS", {"start": v(-14.03, -5.4) * mm, "mid": v(-16.03, -7.4) * mm, "end": v(-14.03, -9.4) * mm});
            skLineSegment(sketch, "E335.MirrorCS", {"start": v(-14.03, -9.4) * mm, "end": v(14.03, -9.4) * mm});
            skLineSegment(sketch, "E336.MirrorCS", {"start": v(-14.03, -27.6) * mm, "end": v(14.03, -27.6) * mm});
            skLineSegment(sketch, "E337.MirrorCS", {"start": v(-14.03, -24.2) * mm, "end": v(14.03, -24.2) * mm});
            skArc(sketch, "E338.MirrorCS", {"start": v(14.03, -31.6) * mm, "mid": v(16.03, -29.6) * mm, "end": v(14.03, -27.6) * mm});
            skLineSegment(sketch, "E339.MirrorCS", {"start": v(-14.03, -7.4) * mm, "end": v(14.03, -7.4) * mm});
            skLineSegment(sketch, "E340.MirrorCS", {"start": v(-14.03, -31.6) * mm, "end": v(14.03, -31.6) * mm});
            skLineSegment(sketch, "E341.MirrorCS", {"start": v(-14.03, -37) * mm, "end": v(14.03, -37) * mm});
            skLineSegment(sketch, "E342.MirrorCS", {"start": v(-14.03, -12.8) * mm, "end": v(14.03, -12.8) * mm});
            skArc(sketch, "E343.MirrorCS", {"start": v(14.03, -24.2) * mm, "mid": v(16.03, -22.2) * mm, "end": v(14.03, -20.2) * mm});
            skLineSegment(sketch, "E344.MirrorCS", {"start": v(-14.03, -20.2) * mm, "end": v(14.03, -20.2) * mm});
            skArc(sketch, "E345.MirrorCS", {"start": v(-14.03, -27.6) * mm, "mid": v(-16.03, -29.6) * mm, "end": v(-14.03, -31.6) * mm});
            skArc(sketch, "E346.MirrorCS", {"start": v(14.03, -9.4) * mm, "mid": v(16.03, -7.4) * mm, "end": v(14.03, -5.4) * mm});
            skLineSegment(sketch, "E347.MirrorCS", {"start": v(-14.03, -14.8) * mm, "end": v(14.03, -14.8) * mm});
            skLineSegment(sketch, "E348.MirrorCS", {"start": v(-14.03, -22.2) * mm, "end": v(14.03, -22.2) * mm});
            skLineSegment(sketch, "E349.MirrorCS", {"start": v(-14.03, -39) * mm, "end": v(14.03, -39) * mm});
            skLineSegment(sketch, "E350.MirrorCS", {"start": v(-14.03, -16.8) * mm, "end": v(14.03, -16.8) * mm});
            skLineSegment(sketch, "E351.MirrorCS", {"start": v(-14.03, -35) * mm, "end": v(14.03, -35) * mm});
            skArc(sketch, "E352.MirrorCS", {"start": v(14.03, -16.8) * mm, "mid": v(16.03, -14.8) * mm, "end": v(14.03, -12.8) * mm});
            skLineSegment(sketch, "E353.MirrorCS", {"start": v(-14.03, -29.6) * mm, "end": v(14.03, -29.6) * mm});
            skLineSegment(sketch, "E354.MirrorCS", {"start": v(-14.03, -5.4) * mm, "end": v(14.03, -5.4) * mm});
            skArc(sketch, "E355.MirrorCS", {"start": v(-14.03, -12.8) * mm, "mid": v(-16.03, -14.8) * mm, "end": v(-14.03, -16.8) * mm});
            skPoint(sketch, "E356.MirrorP", {"position": v(0, -44.4) * mm});
            skLineSegment(sketch, "E357.MirrorCS", {"start": v(-14.03, -42.4) * mm, "end": v(14.03, -42.4) * mm});
            skArc(sketch, "E358.MirrorCS", {"start": v(-14.03, -42.4) * mm, "mid": v(-16.03, -44.4) * mm, "end": v(-14.03, -46.4) * mm});
            skArc(sketch, "E359.MirrorCS", {"start": v(14.03, -46.4) * mm, "mid": v(16.03, -44.4) * mm, "end": v(14.03, -42.4) * mm});
            skLineSegment(sketch, "E360.MirrorCS", {"start": v(-14.03, -46.4) * mm, "end": v(14.03, -46.4) * mm});
            skLineSegment(sketch, "E361.MirrorCS", {"start": v(-14.03, -44.4) * mm, "end": v(14.03, -44.4) * mm});
            skSolve(sketch);
        }
        {
            var Q0;
            Q0 = qSketchRegion(id + "F2", true);
            extrude(context, id + "F3", {"entities" : qUnion([Q0]), "depth" : 2 * mm});
        }
        {
            var Q0;
            Q0=sQuery(id+"F2.wireOp",VERTEX,"E311.rect.right.end");
            var Q1;
            Q1=sQuery(id+"F2.wireOp",VERTEX,"E311.rect.left.end");
            var Q2;
            Q2=sQuery(id+"F2.wireOp",VERTEX,"E311.rect.right.start");
            var Q3;
            Q3=sQuery(id+"F2.wireOp",VERTEX,"E311.rect.left.start");
            var Q4;
            Q4=makeQuery(id+"F3.opExtrude","SWEPT_BODY",BODY,{"disambiguationData":[OSD([sQuery(id+"F2.wireOp",EDGE,"E306.rect.bottom"),sQuery(id+"F2.wireOp",EDGE,"E306.rect.top"),sQuery(id+"F2.wireOp",EDGE,"E306.rect.left"),sQuery(id+"F2.wireOp",EDGE,"E306.rect.right"),sQuery(id+"F2.wireOp",EDGE,"E307.filletArc"),sQuery(id+"F2.wireOp",EDGE,"E308.filletArc"),sQuery(id+"F2.wireOp",EDGE,"E309.filletArc"),sQuery(id+"F2.wireOp",EDGE,"E310.filletArc"),sQuery(id+"F2.wireOp",EDGE,"E314.0.startCap"),sQuery(id+"F2.wireOp",EDGE,"E314.0.endCap"),sQuery(id+"F2.wireOp",EDGE,"E314.0.left"),sQuery(id+"F2.wireOp",EDGE,"E314.0.right"),sQuery(id+"F2.wireOp",EDGE,"E315.0.1.1"),sQuery(id+"F2.wireOp",EDGE,"E315.0.1.2"),sQuery(id+"F2.wireOp",EDGE,"E315.0.1.3"),sQuery(id+"F2.wireOp",EDGE,"E315.0.1.4"),sQuery(id+"F2.wireOp",EDGE,"E315.0.2.1"),sQuery(id+"F2.wireOp",EDGE,"E315.0.2.2"),sQuery(id+"F2.wireOp",EDGE,"E315.0.2.3"),sQuery(id+"F2.wireOp",EDGE,"E315.0.2.4"),sQuery(id+"F2.wireOp",EDGE,"E315.0.3.1"),sQuery(id+"F2.wireOp",EDGE,"E315.0.3.2"),sQuery(id+"F2.wireOp",EDGE,"E315.0.3.3"),sQuery(id+"F2.wireOp",EDGE,"E315.0.3.4"),sQuery(id+"F2.wireOp",EDGE,"E315.0.4.1"),sQuery(id+"F2.wireOp",EDGE,"E315.0.4.2"),sQuery(id+"F2.wireOp",EDGE,"E315.0.4.3"),sQuery(id+"F2.wireOp",EDGE,"E315.0.4.4"),sQuery(id+"F2.wireOp",EDGE,"E315.0.5.1"),sQuery(id+"F2.wireOp",EDGE,"E315.0.5.2"),sQuery(id+"F2.wireOp",EDGE,"E315.0.5.3"),sQuery(id+"F2.wireOp",EDGE,"E315.0.5.4"),sQuery(id+"F2.wireOp",EDGE,"E315.0.6.1"),sQuery(id+"F2.wireOp",EDGE,"E315.0.6.2"),sQuery(id+"F2.wireOp",EDGE,"E315.0.6.3"),sQuery(id+"F2.wireOp",EDGE,"E315.0.6.4"),sQuery(id+"F2.wireOp",EDGE,"f99ec34c-4eab-47e2-88c8-615c967facd713.MirrorCS"),sQuery(id+"F2.wireOp",EDGE,"f99ec34c-4eab-47e2-88c8-615c967facd714.MirrorCS"),sQuery(id+"F2.wireOp",EDGE,"f99ec34c-4eab-47e2-88c8-615c967facd715.MirrorCS"),sQuery(id+"F2.wireOp",EDGE,"f99ec34c-4eab-47e2-88c8-615c967facd716.MirrorCS"),sQuery(id+"F2.wireOp",EDGE,"f99ec34c-4eab-47e2-88c8-615c967facd717.MirrorCS"),sQuery(id+"F2.wireOp",EDGE,"f99ec34c-4eab-47e2-88c8-615c967facd718.MirrorCS"),sQuery(id+"F2.wireOp",EDGE,"f99ec34c-4eab-47e2-88c8-615c967facd720.MirrorCS"),sQuery(id+"F2.wireOp",EDGE,"f99ec34c-4eab-47e2-88c8-615c967facd721.MirrorCS"),sQuery(id+"F2.wireOp",EDGE,"f99ec34c-4eab-47e2-88c8-615c967facd722.MirrorCS"),sQuery(id+"F2.wireOp",EDGE,"f99ec34c-4eab-47e2-88c8-615c967facd725.MirrorCS"),sQuery(id+"F2.wireOp",EDGE,"f99ec34c-4eab-47e2-88c8-615c967facd726.MirrorCS"),sQuery(id+"F2.wireOp",EDGE,"f99ec34c-4eab-47e2-88c8-615c967facd727.MirrorCS"),sQuery(id+"F2.wireOp",EDGE,"f99ec34c-4eab-47e2-88c8-615c967facd729.MirrorCS"),sQuery(id+"F2.wireOp",EDGE,"f99ec34c-4eab-47e2-88c8-615c967facd731.MirrorCS"),sQuery(id+"F2.wireOp",EDGE,"f99ec34c-4eab-47e2-88c8-615c967facd732.MirrorCS"),sQuery(id+"F2.wireOp",EDGE,"f99ec34c-4eab-47e2-88c8-615c967facd733.MirrorCS"),sQuery(id+"F2.wireOp",EDGE,"f99ec34c-4eab-47e2-88c8-615c967facd734.MirrorCS"),sQuery(id+"F2.wireOp",EDGE,"f99ec34c-4eab-47e2-88c8-615c967facd736.MirrorCS"),sQuery(id+"F2.wireOp",EDGE,"f99ec34c-4eab-47e2-88c8-615c967facd739.MirrorCS"),sQuery(id+"F2.wireOp",EDGE,"f99ec34c-4eab-47e2-88c8-615c967facd740.MirrorCS"),sQuery(id+"F2.wireOp",EDGE,"f99ec34c-4eab-47e2-88c8-615c967facd743.MirrorCS"),sQuery(id+"F2.wireOp",EDGE,"f99ec34c-4eab-47e2-88c8-615c967facd744.MirrorCS"),sQuery(id+"F2.wireOp",EDGE,"f99ec34c-4eab-47e2-88c8-615c967facd745.MirrorCS"),sQuery(id+"F2.wireOp",EDGE,"f99ec34c-4eab-47e2-88c8-615c967facd747.MirrorCS"),sQuery(id+"F2.wireOp",EDGE,"E318.0.startCap"),sQuery(id+"F2.wireOp",EDGE,"E318.0.endCap"),sQuery(id+"F2.wireOp",EDGE,"E318.0.left"),sQuery(id+"F2.wireOp",EDGE,"E318.0.right"),sQuery(id+"F2.wireOp",EDGE,"E319.0.startCap"),sQuery(id+"F2.wireOp",EDGE,"E319.0.endCap"),sQuery(id+"F2.wireOp",EDGE,"E319.0.left"),sQuery(id+"F2.wireOp",EDGE,"E319.0.right")])]});
            var Q5;
            Q5=makeQuery(id+"F1.opExtrude","SWEPT_BODY",BODY,{"disambiguationData":[OSD([sQuery(id+"F0.wireOp",EDGE,"E1"),sQuery(id+"F0.wireOp",EDGE,"E2"),sQuery(id+"F0.wireOp",EDGE,"E4"),sQuery(id+"F0.wireOp",EDGE,"E11.0"),sQuery(id+"F0.wireOp",EDGE,"E11.1"),sQuery(id+"F0.wireOp",EDGE,"E11.2"),sQuery(id+"F0.wireOp",EDGE,"E11.3"),sQuery(id+"F0.wireOp",EDGE,"E12.0"),sQuery(id+"F0.wireOp",EDGE,"E12.1"),sQuery(id+"F0.wireOp",EDGE,"E12.2"),sQuery(id+"F0.wireOp",EDGE,"E12.3"),sQuery(id+"F0.wireOp",EDGE,"E13"),sQuery(id+"F0.wireOp",EDGE,"E14"),sQuery(id+"F0.wireOp",EDGE,"E15"),sQuery(id+"F0.wireOp",EDGE,"E16"),sQuery(id+"F0.wireOp",EDGE,"E17.trimOffspring"),sQuery(id+"F0.wireOp",EDGE,"E20.trimOffspring"),sQuery(id+"F0.wireOp",EDGE,"E21.trimOffspring"),sQuery(id+"F0.wireOp",EDGE,"E22.trimOffspring"),sQuery(id+"F0.wireOp",EDGE,"E23.trimOffspring"),sQuery(id+"F0.wireOp",EDGE,"E28.0"),sQuery(id+"F0.wireOp",EDGE,"E29.0"),sQuery(id+"F0.wireOp",EDGE,"E30.0"),sQuery(id+"F0.wireOp",EDGE,"E31.0"),sQuery(id+"F0.wireOp",EDGE,"E32.0"),sQuery(id+"F0.wireOp",EDGE,"E33.0"),sQuery(id+"F0.wireOp",EDGE,"E34.0"),sQuery(id+"F0.wireOp",EDGE,"E35.0"),sQuery(id+"F0.wireOp",EDGE,"E52.trimOffspring"),sQuery(id+"F0.wireOp",EDGE,"E53.filletArc"),sQuery(id+"F0.wireOp",EDGE,"E54.trimOffspring"),sQuery(id+"F0.wireOp",EDGE,"E55.trimOffspring"),sQuery(id+"F0.wireOp",EDGE,"E56.trimOffspring"),sQuery(id+"F0.wireOp",EDGE,"E57.filletArc"),sQuery(id+"F0.wireOp",EDGE,"E58.filletArc"),sQuery(id+"F0.wireOp",EDGE,"E59.filletArc"),sQuery(id+"F0.wireOp",EDGE,"E60.filletArc"),sQuery(id+"F0.wireOp",EDGE,"E61.filletArc"),sQuery(id+"F0.wireOp",EDGE,"E62.filletArc"),sQuery(id+"F0.wireOp",EDGE,"E63.filletArc"),sQuery(id+"F0.wireOp",EDGE,"E66.filletArc"),sQuery(id+"F0.wireOp",EDGE,"E67.filletArc"),sQuery(id+"F0.wireOp",EDGE,"E68.filletArc"),sQuery(id+"F0.wireOp",EDGE,"E69.filletArc"),sQuery(id+"F0.wireOp",EDGE,"E70.filletArc"),sQuery(id+"F0.wireOp",EDGE,"E71.filletArc"),sQuery(id+"F0.wireOp",EDGE,"E72.filletArc"),sQuery(id+"F0.wireOp",EDGE,"E73.filletArc"),sQuery(id+"F0.wireOp",EDGE,"E74.filletArc"),sQuery(id+"F0.wireOp",EDGE,"E75.filletArc"),sQuery(id+"F0.wireOp",EDGE,"E76.filletArc"),sQuery(id+"F0.wireOp",EDGE,"E77.filletArc"),sQuery(id+"F0.wireOp",EDGE,"E78.filletArc"),sQuery(id+"F0.wireOp",EDGE,"E79.filletArc"),sQuery(id+"F0.wireOp",EDGE,"E80.filletArc"),sQuery(id+"F0.wireOp",EDGE,"E81.filletArc"),sQuery(id+"F0.wireOp",EDGE,"E83.filletArc"),sQuery(id+"F0.wireOp",EDGE,"E84.filletArc"),sQuery(id+"F0.wireOp",EDGE,"E85.filletArc"),sQuery(id+"F0.wireOp",EDGE,"E86.filletArc"),sQuery(id+"F0.wireOp",EDGE,"E87.filletArc"),sQuery(id+"F0.wireOp",EDGE,"E88.filletArc"),sQuery(id+"F0.wireOp",EDGE,"E89.filletArc"),sQuery(id+"F0.wireOp",EDGE,"E90.filletArc"),sQuery(id+"F0.wireOp",EDGE,"E91"),sQuery(id+"F0.wireOp",EDGE,"E13"),sQuery(id+"F0.wireOp",EDGE,"E16"),sQuery(id+"F0.wireOp",EDGE,"E92.trimOffspring"),sQuery(id+"F0.wireOp",EDGE,"E93.trimOffspring"),sQuery(id+"F0.wireOp",EDGE,"E94.trimOffspring"),sQuery(id+"F0.wireOp",EDGE,"E95.trimOffspring"),sQuery(id+"F0.wireOp",EDGE,"E96.trimOffspring"),sQuery(id+"F0.wireOp",EDGE,"E97.filletArc"),sQuery(id+"F0.wireOp",EDGE,"E98.filletArc"),sQuery(id+"F0.wireOp",EDGE,"E99.filletArc"),sQuery(id+"F0.wireOp",EDGE,"E100.filletArc"),sQuery(id+"F0.wireOp",EDGE,"E101.filletArc"),sQuery(id+"F0.wireOp",EDGE,"E102.filletArc"),sQuery(id+"F0.wireOp",EDGE,"E103.filletArc"),sQuery(id+"F0.wireOp",EDGE,"E104.filletArc"),sQuery(id+"F0.wireOp",EDGE,"E105"),sQuery(id+"F0.wireOp",EDGE,"E106"),sQuery(id+"F0.wireOp",EDGE,"E107"),sQuery(id+"F0.wireOp",EDGE,"E108"),sQuery(id+"F0.wireOp",EDGE,"E109"),sQuery(id+"F0.wireOp",EDGE,"E113.MirrorC"),sQuery(id+"F0.wireOp",EDGE,"E110"),sQuery(id+"F0.wireOp",EDGE,"E114.MirrorC"),sQuery(id+"F0.wireOp",EDGE,"E115.filletArc"),sQuery(id+"F0.wireOp",EDGE,"E116.filletArc"),sQuery(id+"F0.wireOp",EDGE,"E117.filletArc"),sQuery(id+"F0.wireOp",EDGE,"E118.filletArc"),sQuery(id+"F0.wireOp",EDGE,"E119.filletArc"),sQuery(id+"F0.wireOp",EDGE,"E120.filletArc"),sQuery(id+"F0.wireOp",EDGE,"E121.filletArc"),sQuery(id+"F0.wireOp",EDGE,"E122.filletArc"),sQuery(id+"F0.wireOp",EDGE,"E123.filletArc"),sQuery(id+"F0.wireOp",EDGE,"E124.filletArc"),sQuery(id+"F0.wireOp",EDGE,"E125.filletArc"),sQuery(id+"F0.wireOp",EDGE,"E126.filletArc"),sQuery(id+"F0.wireOp",EDGE,"E127"),sQuery(id+"F0.wireOp",EDGE,"E128"),sQuery(id+"F0.wireOp",EDGE,"E129"),sQuery(id+"F0.wireOp",EDGE,"E134"),sQuery(id+"F0.wireOp",EDGE,"E135"),sQuery(id+"F0.wireOp",EDGE,"E136.trimOffspring"),sQuery(id+"F0.wireOp",EDGE,"E137.trimOffspring"),sQuery(id+"F0.wireOp",EDGE,"E138.trimOffspring"),sQuery(id+"F0.wireOp",EDGE,"E139.filletArc"),sQuery(id+"F0.wireOp",EDGE,"E140.filletArc"),sQuery(id+"F0.wireOp",EDGE,"E141.filletArc"),sQuery(id+"F0.wireOp",EDGE,"E142.filletArc"),sQuery(id+"F0.wireOp",EDGE,"E143.trimOffspring"),sQuery(id+"F0.wireOp",EDGE,"E144.trimOffspring"),sQuery(id+"F0.wireOp",EDGE,"E145.trimOffspring"),sQuery(id+"F0.wireOp",EDGE,"E146.filletArc"),sQuery(id+"F0.wireOp",EDGE,"E147.filletArc"),sQuery(id+"F0.wireOp",EDGE,"E148.filletArc"),sQuery(id+"F0.wireOp",EDGE,"E149.filletArc"),sQuery(id+"F0.wireOp",EDGE,"E150"),sQuery(id+"F0.wireOp",EDGE,"E151"),sQuery(id+"F0.wireOp",EDGE,"E152"),sQuery(id+"F0.wireOp",EDGE,"E153"),sQuery(id+"F0.wireOp",EDGE,"E154"),sQuery(id+"F0.wireOp",EDGE,"E155"),sQuery(id+"F0.wireOp",EDGE,"E156"),sQuery(id+"F0.wireOp",EDGE,"E157"),sQuery(id+"F0.wireOp",EDGE,"E158"),sQuery(id+"F0.wireOp",EDGE,"E159"),sQuery(id+"F0.wireOp",EDGE,"E160"),sQuery(id+"F0.wireOp",EDGE,"E161.MirrorCS"),sQuery(id+"F0.wireOp",EDGE,"E162.MirrorCS"),sQuery(id+"F0.wireOp",EDGE,"E163.MirrorC"),sQuery(id+"F0.wireOp",EDGE,"E164.MirrorCS"),sQuery(id+"F0.wireOp",EDGE,"E165.MirrorCS"),sQuery(id+"F0.wireOp",EDGE,"E166.MirrorCS"),sQuery(id+"F0.wireOp",EDGE,"E167.MirrorCS"),sQuery(id+"F0.wireOp",EDGE,"E168.MirrorC"),sQuery(id+"F0.wireOp",EDGE,"E169.MirrorCS"),sQuery(id+"F0.wireOp",EDGE,"E170.MirrorCS"),sQuery(id+"F0.wireOp",EDGE,"E171.MirrorCS"),sQuery(id+"F0.wireOp",EDGE,"E172.MirrorCS"),sQuery(id+"F0.wireOp",EDGE,"E173.MirrorCS"),sQuery(id+"F0.wireOp",EDGE,"E174.MirrorCS"),sQuery(id+"F0.wireOp",EDGE,"E176"),sQuery(id+"F0.wireOp",EDGE,"E177"),sQuery(id+"F0.wireOp",EDGE,"E178.trimOffspring"),sQuery(id+"F0.wireOp",EDGE,"E179.filletArc"),sQuery(id+"F0.wireOp",EDGE,"E180.filletArc"),sQuery(id+"F0.wireOp",EDGE,"E181.MirrorC"),sQuery(id+"F0.wireOp",EDGE,"E182.MirrorCS"),sQuery(id+"F0.wireOp",EDGE,"E183.MirrorCS"),sQuery(id+"F0.wireOp",EDGE,"E184.MirrorCS"),sQuery(id+"F0.wireOp",EDGE,"E185.trimOffspring"),sQuery(id+"F0.wireOp",EDGE,"E186.trimOffspring"),sQuery(id+"F0.wireOp",EDGE,"E187.trimOffspring"),sQuery(id+"F0.wireOp",EDGE,"E188.trimOffspring"),sQuery(id+"F0.wireOp",EDGE,"E189.trimOffspring"),sQuery(id+"F0.wireOp",EDGE,"E190.MirrorCS"),sQuery(id+"F0.wireOp",EDGE,"E191.MirrorCS"),sQuery(id+"F0.wireOp",EDGE,"E192.MirrorCS"),sQuery(id+"F0.wireOp",EDGE,"E193.MirrorCS"),sQuery(id+"F0.wireOp",EDGE,"E194.MirrorCS"),sQuery(id+"F0.wireOp",EDGE,"E195.MirrorCS"),sQuery(id+"F0.wireOp",EDGE,"E196.MirrorCS"),sQuery(id+"F0.wireOp",EDGE,"E197.MirrorCS"),sQuery(id+"F0.wireOp",EDGE,"E198.MirrorCS"),sQuery(id+"F0.wireOp",EDGE,"E199.MirrorCS"),sQuery(id+"F0.wireOp",EDGE,"E200.MirrorCS"),sQuery(id+"F0.wireOp",EDGE,"E201.MirrorCS"),sQuery(id+"F0.wireOp",EDGE,"E202.MirrorCS"),sQuery(id+"F0.wireOp",EDGE,"E203.MirrorCS"),sQuery(id+"F0.wireOp",EDGE,"E204.MirrorCS"),sQuery(id+"F0.wireOp",EDGE,"E205.MirrorCS"),sQuery(id+"F0.wireOp",EDGE,"E206.MirrorCS"),sQuery(id+"F0.wireOp",EDGE,"E207.MirrorCS"),sQuery(id+"F0.wireOp",EDGE,"E208.MirrorCS"),sQuery(id+"F0.wireOp",EDGE,"E209.MirrorCS"),sQuery(id+"F0.wireOp",EDGE,"E210.MirrorC"),sQuery(id+"F0.wireOp",EDGE,"E211.MirrorC"),sQuery(id+"F0.wireOp",EDGE,"E212.MirrorC"),sQuery(id+"F0.wireOp",EDGE,"E213.MirrorC"),sQuery(id+"F0.wireOp",EDGE,"E214.MirrorC"),sQuery(id+"F0.wireOp",EDGE,"E215.MirrorCS"),sQuery(id+"F0.wireOp",EDGE,"E216.MirrorCS"),sQuery(id+"F0.wireOp",EDGE,"E217.MirrorCS"),sQuery(id+"F0.wireOp",EDGE,"E218.MirrorCS"),sQuery(id+"F0.wireOp",EDGE,"E219.MirrorCS"),sQuery(id+"F0.wireOp",EDGE,"E220.MirrorCS"),sQuery(id+"F0.wireOp",EDGE,"E221.MirrorC"),sQuery(id+"F0.wireOp",EDGE,"E222.MirrorCS"),sQuery(id+"F0.wireOp",EDGE,"E223.MirrorCS"),sQuery(id+"F0.wireOp",EDGE,"E224.MirrorCS"),sQuery(id+"F0.wireOp",EDGE,"E225.trimOffspring"),sQuery(id+"F0.wireOp",EDGE,"E226.trimOffspring"),sQuery(id+"F0.wireOp",EDGE,"E227.trimOffspring"),sQuery(id+"F0.wireOp",EDGE,"E228.trimOffspring"),sQuery(id+"F0.wireOp",EDGE,"E229.trimOffspring"),sQuery(id+"F0.wireOp",EDGE,"E230.trimOffspring"),sQuery(id+"F0.wireOp",EDGE,"E231.MirrorCS"),sQuery(id+"F0.wireOp",EDGE,"E232.trimOffspring"),sQuery(id+"F0.wireOp",EDGE,"E233.trimOffspring"),sQuery(id+"F0.wireOp",EDGE,"E234.trimOffspring"),sQuery(id+"F0.wireOp",EDGE,"E235.trimOffspring"),sQuery(id+"F0.wireOp",EDGE,"E239"),sQuery(id+"F0.wireOp",EDGE,"E241"),sQuery(id+"F0.wireOp",EDGE,"E242.MirrorC"),sQuery(id+"F0.wireOp",EDGE,"E243.MirrorC"),sQuery(id+"F0.wireOp",EDGE,"E245"),sQuery(id+"F0.wireOp",EDGE,"E246"),sQuery(id+"F0.wireOp",EDGE,"E247"),sQuery(id+"F0.wireOp",EDGE,"E248"),sQuery(id+"F0.wireOp",EDGE,"E255.0.startCap"),sQuery(id+"F0.wireOp",EDGE,"E255.0.endCap"),sQuery(id+"F0.wireOp",EDGE,"E255.0.left"),sQuery(id+"F0.wireOp",EDGE,"E255.0.right"),sQuery(id+"F0.wireOp",EDGE,"E256.0.startCap"),sQuery(id+"F0.wireOp",EDGE,"E256.0.endCap"),sQuery(id+"F0.wireOp",EDGE,"E256.0.left"),sQuery(id+"F0.wireOp",EDGE,"E256.0.right"),sQuery(id+"F0.wireOp",EDGE,"E257.0.startCap"),sQuery(id+"F0.wireOp",EDGE,"E257.0.endCap"),sQuery(id+"F0.wireOp",EDGE,"E257.0.left"),sQuery(id+"F0.wireOp",EDGE,"E257.0.right"),sQuery(id+"F0.wireOp",EDGE,"E257.1.startCap"),sQuery(id+"F0.wireOp",EDGE,"E257.1.endCap"),sQuery(id+"F0.wireOp",EDGE,"E257.1.left"),sQuery(id+"F0.wireOp",EDGE,"E257.1.right"),sQuery(id+"F0.wireOp",EDGE,"E258.MirrorCS"),sQuery(id+"F0.wireOp",EDGE,"E259.MirrorCS"),sQuery(id+"F0.wireOp",EDGE,"E260.MirrorCS"),sQuery(id+"F0.wireOp",EDGE,"E261.MirrorCS"),sQuery(id+"F0.wireOp",EDGE,"E262.MirrorCS"),sQuery(id+"F0.wireOp",EDGE,"E263.MirrorCS"),sQuery(id+"F0.wireOp",EDGE,"E264.MirrorCS"),sQuery(id+"F0.wireOp",EDGE,"E265.MirrorCS"),sQuery(id+"F0.wireOp",EDGE,"E266.MirrorCS"),sQuery(id+"F0.wireOp",EDGE,"E267.MirrorCS"),sQuery(id+"F0.wireOp",EDGE,"E268.MirrorCS"),sQuery(id+"F0.wireOp",EDGE,"E269.MirrorCS"),sQuery(id+"F0.wireOp",EDGE,"E270.MirrorCS"),sQuery(id+"F0.wireOp",EDGE,"E271.MirrorCS"),sQuery(id+"F0.wireOp",EDGE,"E272.MirrorCS"),sQuery(id+"F0.wireOp",EDGE,"E273.MirrorCS"),sQuery(id+"F0.wireOp",EDGE,"E274.MirrorCS"),sQuery(id+"F0.wireOp",EDGE,"E275.MirrorCS"),sQuery(id+"F0.wireOp",EDGE,"E276.MirrorCS"),sQuery(id+"F0.wireOp",EDGE,"E277.MirrorCS"),sQuery(id+"F0.wireOp",EDGE,"E278.MirrorCS"),sQuery(id+"F0.wireOp",EDGE,"E279.MirrorCS"),sQuery(id+"F0.wireOp",EDGE,"E280.MirrorCS"),sQuery(id+"F0.wireOp",EDGE,"E281.MirrorCS"),sQuery(id+"F0.wireOp",EDGE,"E282.MirrorCS"),sQuery(id+"F0.wireOp",EDGE,"E283.MirrorCS"),sQuery(id+"F0.wireOp",EDGE,"E284.MirrorCS"),sQuery(id+"F0.wireOp",EDGE,"E285.MirrorCS"),sQuery(id+"F0.wireOp",EDGE,"E286.MirrorCS"),sQuery(id+"F0.wireOp",EDGE,"E287.MirrorCS"),sQuery(id+"F0.wireOp",EDGE,"E288.MirrorCS"),sQuery(id+"F0.wireOp",EDGE,"E289.MirrorCS"),sQuery(id+"F0.wireOp",EDGE,"E290.MirrorCS"),sQuery(id+"F0.wireOp",EDGE,"E291.MirrorCS"),sQuery(id+"F0.wireOp",EDGE,"E292.MirrorCS"),sQuery(id+"F0.wireOp",EDGE,"E293.MirrorCS"),sQuery(id+"F0.wireOp",EDGE,"E294.MirrorCS"),sQuery(id+"F0.wireOp",EDGE,"E295.MirrorCS"),sQuery(id+"F0.wireOp",EDGE,"E296.MirrorCS"),sQuery(id+"F0.wireOp",EDGE,"E297.MirrorCS"),sQuery(id+"F0.wireOp",EDGE,"E298.MirrorCS"),sQuery(id+"F0.wireOp",EDGE,"E299.MirrorCS"),sQuery(id+"F0.wireOp",EDGE,"E300.MirrorCS"),sQuery(id+"F0.wireOp",EDGE,"E301.MirrorCS"),sQuery(id+"F0.wireOp",EDGE,"E302.MirrorCS"),sQuery(id+"F0.wireOp",EDGE,"E303.MirrorCS"),sQuery(id+"F0.wireOp",EDGE,"E304.MirrorCS"),sQuery(id+"F0.wireOp",EDGE,"E305")])]});
            hole(context, id + "F4", {"style" : HoleStyle.SIMPLE, "holeDiameter" : 3 * mm, "endStyle" : HoleEndStyle.THROUGH, "oppositeDirection" : true, "locations" : qUnion([Q0, Q1, Q2, Q3]), "scope" : qUnion([Q4, Q5])});
        }
        {
            var Q0;
            Q0=sQuery(id+"F2.wireOp",VERTEX,"E311.rect.right.end");
            var Q1;
            Q1=sQuery(id+"F2.wireOp",VERTEX,"E311.rect.left.end");
            var Q2;
            Q2=sQuery(id+"F2.wireOp",VERTEX,"E311.rect.left.start");
            var Q3;
            Q3=sQuery(id+"F2.wireOp",VERTEX,"E311.rect.right.start");
            var Q4;
            Q4=makeQuery(id+"F1.opExtrude","SWEPT_BODY",BODY,{"disambiguationData":[OSD([sQuery(id+"F0.wireOp",EDGE,"E1"),sQuery(id+"F0.wireOp",EDGE,"E2"),sQuery(id+"F0.wireOp",EDGE,"E4"),sQuery(id+"F0.wireOp",EDGE,"E11.0"),sQuery(id+"F0.wireOp",EDGE,"E11.1"),sQuery(id+"F0.wireOp",EDGE,"E11.2"),sQuery(id+"F0.wireOp",EDGE,"E11.3"),sQuery(id+"F0.wireOp",EDGE,"E12.0"),sQuery(id+"F0.wireOp",EDGE,"E12.1"),sQuery(id+"F0.wireOp",EDGE,"E12.2"),sQuery(id+"F0.wireOp",EDGE,"E12.3"),sQuery(id+"F0.wireOp",EDGE,"E13"),sQuery(id+"F0.wireOp",EDGE,"E14"),sQuery(id+"F0.wireOp",EDGE,"E15"),sQuery(id+"F0.wireOp",EDGE,"E16"),sQuery(id+"F0.wireOp",EDGE,"E17.trimOffspring"),sQuery(id+"F0.wireOp",EDGE,"E20.trimOffspring"),sQuery(id+"F0.wireOp",EDGE,"E21.trimOffspring"),sQuery(id+"F0.wireOp",EDGE,"E22.trimOffspring"),sQuery(id+"F0.wireOp",EDGE,"E23.trimOffspring"),sQuery(id+"F0.wireOp",EDGE,"E28.0"),sQuery(id+"F0.wireOp",EDGE,"E29.0"),sQuery(id+"F0.wireOp",EDGE,"E30.0"),sQuery(id+"F0.wireOp",EDGE,"E31.0"),sQuery(id+"F0.wireOp",EDGE,"E32.0"),sQuery(id+"F0.wireOp",EDGE,"E33.0"),sQuery(id+"F0.wireOp",EDGE,"E34.0"),sQuery(id+"F0.wireOp",EDGE,"E35.0"),sQuery(id+"F0.wireOp",EDGE,"E52.trimOffspring"),sQuery(id+"F0.wireOp",EDGE,"E53.filletArc"),sQuery(id+"F0.wireOp",EDGE,"E54.trimOffspring"),sQuery(id+"F0.wireOp",EDGE,"E55.trimOffspring"),sQuery(id+"F0.wireOp",EDGE,"E56.trimOffspring"),sQuery(id+"F0.wireOp",EDGE,"E57.filletArc"),sQuery(id+"F0.wireOp",EDGE,"E58.filletArc"),sQuery(id+"F0.wireOp",EDGE,"E59.filletArc"),sQuery(id+"F0.wireOp",EDGE,"E60.filletArc"),sQuery(id+"F0.wireOp",EDGE,"E61.filletArc"),sQuery(id+"F0.wireOp",EDGE,"E62.filletArc"),sQuery(id+"F0.wireOp",EDGE,"E63.filletArc"),sQuery(id+"F0.wireOp",EDGE,"E66.filletArc"),sQuery(id+"F0.wireOp",EDGE,"E67.filletArc"),sQuery(id+"F0.wireOp",EDGE,"E68.filletArc"),sQuery(id+"F0.wireOp",EDGE,"E69.filletArc"),sQuery(id+"F0.wireOp",EDGE,"E70.filletArc"),sQuery(id+"F0.wireOp",EDGE,"E71.filletArc"),sQuery(id+"F0.wireOp",EDGE,"E72.filletArc"),sQuery(id+"F0.wireOp",EDGE,"E73.filletArc"),sQuery(id+"F0.wireOp",EDGE,"E74.filletArc"),sQuery(id+"F0.wireOp",EDGE,"E75.filletArc"),sQuery(id+"F0.wireOp",EDGE,"E76.filletArc"),sQuery(id+"F0.wireOp",EDGE,"E77.filletArc"),sQuery(id+"F0.wireOp",EDGE,"E78.filletArc"),sQuery(id+"F0.wireOp",EDGE,"E79.filletArc"),sQuery(id+"F0.wireOp",EDGE,"E80.filletArc"),sQuery(id+"F0.wireOp",EDGE,"E81.filletArc"),sQuery(id+"F0.wireOp",EDGE,"E83.filletArc"),sQuery(id+"F0.wireOp",EDGE,"E84.filletArc"),sQuery(id+"F0.wireOp",EDGE,"E85.filletArc"),sQuery(id+"F0.wireOp",EDGE,"E86.filletArc"),sQuery(id+"F0.wireOp",EDGE,"E87.filletArc"),sQuery(id+"F0.wireOp",EDGE,"E88.filletArc"),sQuery(id+"F0.wireOp",EDGE,"E89.filletArc"),sQuery(id+"F0.wireOp",EDGE,"E90.filletArc"),sQuery(id+"F0.wireOp",EDGE,"E91"),sQuery(id+"F0.wireOp",EDGE,"E13"),sQuery(id+"F0.wireOp",EDGE,"E16"),sQuery(id+"F0.wireOp",EDGE,"E92.trimOffspring"),sQuery(id+"F0.wireOp",EDGE,"E93.trimOffspring"),sQuery(id+"F0.wireOp",EDGE,"E94.trimOffspring"),sQuery(id+"F0.wireOp",EDGE,"E95.trimOffspring"),sQuery(id+"F0.wireOp",EDGE,"E96.trimOffspring"),sQuery(id+"F0.wireOp",EDGE,"E97.filletArc"),sQuery(id+"F0.wireOp",EDGE,"E98.filletArc"),sQuery(id+"F0.wireOp",EDGE,"E99.filletArc"),sQuery(id+"F0.wireOp",EDGE,"E100.filletArc"),sQuery(id+"F0.wireOp",EDGE,"E101.filletArc"),sQuery(id+"F0.wireOp",EDGE,"E102.filletArc"),sQuery(id+"F0.wireOp",EDGE,"E103.filletArc"),sQuery(id+"F0.wireOp",EDGE,"E104.filletArc"),sQuery(id+"F0.wireOp",EDGE,"E105"),sQuery(id+"F0.wireOp",EDGE,"E106"),sQuery(id+"F0.wireOp",EDGE,"E107"),sQuery(id+"F0.wireOp",EDGE,"E108"),sQuery(id+"F0.wireOp",EDGE,"E109"),sQuery(id+"F0.wireOp",EDGE,"E113.MirrorC"),sQuery(id+"F0.wireOp",EDGE,"E110"),sQuery(id+"F0.wireOp",EDGE,"E114.MirrorC"),sQuery(id+"F0.wireOp",EDGE,"E115.filletArc"),sQuery(id+"F0.wireOp",EDGE,"E116.filletArc"),sQuery(id+"F0.wireOp",EDGE,"E117.filletArc"),sQuery(id+"F0.wireOp",EDGE,"E118.filletArc"),sQuery(id+"F0.wireOp",EDGE,"E119.filletArc"),sQuery(id+"F0.wireOp",EDGE,"E120.filletArc"),sQuery(id+"F0.wireOp",EDGE,"E121.filletArc"),sQuery(id+"F0.wireOp",EDGE,"E122.filletArc"),sQuery(id+"F0.wireOp",EDGE,"E123.filletArc"),sQuery(id+"F0.wireOp",EDGE,"E124.filletArc"),sQuery(id+"F0.wireOp",EDGE,"E125.filletArc"),sQuery(id+"F0.wireOp",EDGE,"E126.filletArc"),sQuery(id+"F0.wireOp",EDGE,"E127"),sQuery(id+"F0.wireOp",EDGE,"E128"),sQuery(id+"F0.wireOp",EDGE,"E129"),sQuery(id+"F0.wireOp",EDGE,"E134"),sQuery(id+"F0.wireOp",EDGE,"E135"),sQuery(id+"F0.wireOp",EDGE,"E136.trimOffspring"),sQuery(id+"F0.wireOp",EDGE,"E137.trimOffspring"),sQuery(id+"F0.wireOp",EDGE,"E138.trimOffspring"),sQuery(id+"F0.wireOp",EDGE,"E139.filletArc"),sQuery(id+"F0.wireOp",EDGE,"E140.filletArc"),sQuery(id+"F0.wireOp",EDGE,"E141.filletArc"),sQuery(id+"F0.wireOp",EDGE,"E142.filletArc"),sQuery(id+"F0.wireOp",EDGE,"E143.trimOffspring"),sQuery(id+"F0.wireOp",EDGE,"E144.trimOffspring"),sQuery(id+"F0.wireOp",EDGE,"E145.trimOffspring"),sQuery(id+"F0.wireOp",EDGE,"E146.filletArc"),sQuery(id+"F0.wireOp",EDGE,"E147.filletArc"),sQuery(id+"F0.wireOp",EDGE,"E148.filletArc"),sQuery(id+"F0.wireOp",EDGE,"E149.filletArc"),sQuery(id+"F0.wireOp",EDGE,"E150"),sQuery(id+"F0.wireOp",EDGE,"E151"),sQuery(id+"F0.wireOp",EDGE,"E152"),sQuery(id+"F0.wireOp",EDGE,"E153"),sQuery(id+"F0.wireOp",EDGE,"E154"),sQuery(id+"F0.wireOp",EDGE,"E155"),sQuery(id+"F0.wireOp",EDGE,"E156"),sQuery(id+"F0.wireOp",EDGE,"E157"),sQuery(id+"F0.wireOp",EDGE,"E158"),sQuery(id+"F0.wireOp",EDGE,"E159"),sQuery(id+"F0.wireOp",EDGE,"E160"),sQuery(id+"F0.wireOp",EDGE,"E161.MirrorCS"),sQuery(id+"F0.wireOp",EDGE,"E162.MirrorCS"),sQuery(id+"F0.wireOp",EDGE,"E163.MirrorC"),sQuery(id+"F0.wireOp",EDGE,"E164.MirrorCS"),sQuery(id+"F0.wireOp",EDGE,"E165.MirrorCS"),sQuery(id+"F0.wireOp",EDGE,"E166.MirrorCS"),sQuery(id+"F0.wireOp",EDGE,"E167.MirrorCS"),sQuery(id+"F0.wireOp",EDGE,"E168.MirrorC"),sQuery(id+"F0.wireOp",EDGE,"E169.MirrorCS"),sQuery(id+"F0.wireOp",EDGE,"E170.MirrorCS"),sQuery(id+"F0.wireOp",EDGE,"E171.MirrorCS"),sQuery(id+"F0.wireOp",EDGE,"E172.MirrorCS"),sQuery(id+"F0.wireOp",EDGE,"E173.MirrorCS"),sQuery(id+"F0.wireOp",EDGE,"E174.MirrorCS"),sQuery(id+"F0.wireOp",EDGE,"E176"),sQuery(id+"F0.wireOp",EDGE,"E177"),sQuery(id+"F0.wireOp",EDGE,"E178.trimOffspring"),sQuery(id+"F0.wireOp",EDGE,"E179.filletArc"),sQuery(id+"F0.wireOp",EDGE,"E180.filletArc"),sQuery(id+"F0.wireOp",EDGE,"E181.MirrorC"),sQuery(id+"F0.wireOp",EDGE,"E182.MirrorCS"),sQuery(id+"F0.wireOp",EDGE,"E183.MirrorCS"),sQuery(id+"F0.wireOp",EDGE,"E184.MirrorCS"),sQuery(id+"F0.wireOp",EDGE,"E185.trimOffspring"),sQuery(id+"F0.wireOp",EDGE,"E186.trimOffspring"),sQuery(id+"F0.wireOp",EDGE,"E187.trimOffspring"),sQuery(id+"F0.wireOp",EDGE,"E188.trimOffspring"),sQuery(id+"F0.wireOp",EDGE,"E189.trimOffspring"),sQuery(id+"F0.wireOp",EDGE,"E190.MirrorCS"),sQuery(id+"F0.wireOp",EDGE,"E191.MirrorCS"),sQuery(id+"F0.wireOp",EDGE,"E192.MirrorCS"),sQuery(id+"F0.wireOp",EDGE,"E193.MirrorCS"),sQuery(id+"F0.wireOp",EDGE,"E194.MirrorCS"),sQuery(id+"F0.wireOp",EDGE,"E195.MirrorCS"),sQuery(id+"F0.wireOp",EDGE,"E196.MirrorCS"),sQuery(id+"F0.wireOp",EDGE,"E197.MirrorCS"),sQuery(id+"F0.wireOp",EDGE,"E198.MirrorCS"),sQuery(id+"F0.wireOp",EDGE,"E199.MirrorCS"),sQuery(id+"F0.wireOp",EDGE,"E200.MirrorCS"),sQuery(id+"F0.wireOp",EDGE,"E201.MirrorCS"),sQuery(id+"F0.wireOp",EDGE,"E202.MirrorCS"),sQuery(id+"F0.wireOp",EDGE,"E203.MirrorCS"),sQuery(id+"F0.wireOp",EDGE,"E204.MirrorCS"),sQuery(id+"F0.wireOp",EDGE,"E205.MirrorCS"),sQuery(id+"F0.wireOp",EDGE,"E206.MirrorCS"),sQuery(id+"F0.wireOp",EDGE,"E207.MirrorCS"),sQuery(id+"F0.wireOp",EDGE,"E208.MirrorCS"),sQuery(id+"F0.wireOp",EDGE,"E209.MirrorCS"),sQuery(id+"F0.wireOp",EDGE,"E210.MirrorC"),sQuery(id+"F0.wireOp",EDGE,"E211.MirrorC"),sQuery(id+"F0.wireOp",EDGE,"E212.MirrorC"),sQuery(id+"F0.wireOp",EDGE,"E213.MirrorC"),sQuery(id+"F0.wireOp",EDGE,"E214.MirrorC"),sQuery(id+"F0.wireOp",EDGE,"E215.MirrorCS"),sQuery(id+"F0.wireOp",EDGE,"E216.MirrorCS"),sQuery(id+"F0.wireOp",EDGE,"E217.MirrorCS"),sQuery(id+"F0.wireOp",EDGE,"E218.MirrorCS"),sQuery(id+"F0.wireOp",EDGE,"E219.MirrorCS"),sQuery(id+"F0.wireOp",EDGE,"E220.MirrorCS"),sQuery(id+"F0.wireOp",EDGE,"E221.MirrorC"),sQuery(id+"F0.wireOp",EDGE,"E222.MirrorCS"),sQuery(id+"F0.wireOp",EDGE,"E223.MirrorCS"),sQuery(id+"F0.wireOp",EDGE,"E224.MirrorCS"),sQuery(id+"F0.wireOp",EDGE,"E225.trimOffspring"),sQuery(id+"F0.wireOp",EDGE,"E226.trimOffspring"),sQuery(id+"F0.wireOp",EDGE,"E227.trimOffspring"),sQuery(id+"F0.wireOp",EDGE,"E228.trimOffspring"),sQuery(id+"F0.wireOp",EDGE,"E229.trimOffspring"),sQuery(id+"F0.wireOp",EDGE,"E230.trimOffspring"),sQuery(id+"F0.wireOp",EDGE,"E231.MirrorCS"),sQuery(id+"F0.wireOp",EDGE,"E232.trimOffspring"),sQuery(id+"F0.wireOp",EDGE,"E233.trimOffspring"),sQuery(id+"F0.wireOp",EDGE,"E234.trimOffspring"),sQuery(id+"F0.wireOp",EDGE,"E235.trimOffspring"),sQuery(id+"F0.wireOp",EDGE,"E239"),sQuery(id+"F0.wireOp",EDGE,"E241"),sQuery(id+"F0.wireOp",EDGE,"E242.MirrorC"),sQuery(id+"F0.wireOp",EDGE,"E243.MirrorC"),sQuery(id+"F0.wireOp",EDGE,"E245"),sQuery(id+"F0.wireOp",EDGE,"E246"),sQuery(id+"F0.wireOp",EDGE,"E247"),sQuery(id+"F0.wireOp",EDGE,"E248"),sQuery(id+"F0.wireOp",EDGE,"E255.0.startCap"),sQuery(id+"F0.wireOp",EDGE,"E255.0.endCap"),sQuery(id+"F0.wireOp",EDGE,"E255.0.left"),sQuery(id+"F0.wireOp",EDGE,"E255.0.right"),sQuery(id+"F0.wireOp",EDGE,"E256.0.startCap"),sQuery(id+"F0.wireOp",EDGE,"E256.0.endCap"),sQuery(id+"F0.wireOp",EDGE,"E256.0.left"),sQuery(id+"F0.wireOp",EDGE,"E256.0.right"),sQuery(id+"F0.wireOp",EDGE,"E257.0.startCap"),sQuery(id+"F0.wireOp",EDGE,"E257.0.endCap"),sQuery(id+"F0.wireOp",EDGE,"E257.0.left"),sQuery(id+"F0.wireOp",EDGE,"E257.0.right"),sQuery(id+"F0.wireOp",EDGE,"E257.1.startCap"),sQuery(id+"F0.wireOp",EDGE,"E257.1.endCap"),sQuery(id+"F0.wireOp",EDGE,"E257.1.left"),sQuery(id+"F0.wireOp",EDGE,"E257.1.right"),sQuery(id+"F0.wireOp",EDGE,"E258.MirrorCS"),sQuery(id+"F0.wireOp",EDGE,"E259.MirrorCS"),sQuery(id+"F0.wireOp",EDGE,"E260.MirrorCS"),sQuery(id+"F0.wireOp",EDGE,"E261.MirrorCS"),sQuery(id+"F0.wireOp",EDGE,"E262.MirrorCS"),sQuery(id+"F0.wireOp",EDGE,"E263.MirrorCS"),sQuery(id+"F0.wireOp",EDGE,"E264.MirrorCS"),sQuery(id+"F0.wireOp",EDGE,"E265.MirrorCS"),sQuery(id+"F0.wireOp",EDGE,"E266.MirrorCS"),sQuery(id+"F0.wireOp",EDGE,"E267.MirrorCS"),sQuery(id+"F0.wireOp",EDGE,"E268.MirrorCS"),sQuery(id+"F0.wireOp",EDGE,"E269.MirrorCS"),sQuery(id+"F0.wireOp",EDGE,"E270.MirrorCS"),sQuery(id+"F0.wireOp",EDGE,"E271.MirrorCS"),sQuery(id+"F0.wireOp",EDGE,"E272.MirrorCS"),sQuery(id+"F0.wireOp",EDGE,"E273.MirrorCS"),sQuery(id+"F0.wireOp",EDGE,"E274.MirrorCS"),sQuery(id+"F0.wireOp",EDGE,"E275.MirrorCS"),sQuery(id+"F0.wireOp",EDGE,"E276.MirrorCS"),sQuery(id+"F0.wireOp",EDGE,"E277.MirrorCS"),sQuery(id+"F0.wireOp",EDGE,"E278.MirrorCS"),sQuery(id+"F0.wireOp",EDGE,"E279.MirrorCS"),sQuery(id+"F0.wireOp",EDGE,"E280.MirrorCS"),sQuery(id+"F0.wireOp",EDGE,"E281.MirrorCS"),sQuery(id+"F0.wireOp",EDGE,"E282.MirrorCS"),sQuery(id+"F0.wireOp",EDGE,"E283.MirrorCS"),sQuery(id+"F0.wireOp",EDGE,"E284.MirrorCS"),sQuery(id+"F0.wireOp",EDGE,"E285.MirrorCS"),sQuery(id+"F0.wireOp",EDGE,"E286.MirrorCS"),sQuery(id+"F0.wireOp",EDGE,"E287.MirrorCS"),sQuery(id+"F0.wireOp",EDGE,"E288.MirrorCS"),sQuery(id+"F0.wireOp",EDGE,"E289.MirrorCS"),sQuery(id+"F0.wireOp",EDGE,"E290.MirrorCS"),sQuery(id+"F0.wireOp",EDGE,"E291.MirrorCS"),sQuery(id+"F0.wireOp",EDGE,"E292.MirrorCS"),sQuery(id+"F0.wireOp",EDGE,"E293.MirrorCS"),sQuery(id+"F0.wireOp",EDGE,"E294.MirrorCS"),sQuery(id+"F0.wireOp",EDGE,"E295.MirrorCS"),sQuery(id+"F0.wireOp",EDGE,"E296.MirrorCS"),sQuery(id+"F0.wireOp",EDGE,"E297.MirrorCS"),sQuery(id+"F0.wireOp",EDGE,"E298.MirrorCS"),sQuery(id+"F0.wireOp",EDGE,"E299.MirrorCS"),sQuery(id+"F0.wireOp",EDGE,"E300.MirrorCS"),sQuery(id+"F0.wireOp",EDGE,"E301.MirrorCS"),sQuery(id+"F0.wireOp",EDGE,"E302.MirrorCS"),sQuery(id+"F0.wireOp",EDGE,"E303.MirrorCS"),sQuery(id+"F0.wireOp",EDGE,"E304.MirrorCS"),sQuery(id+"F0.wireOp",EDGE,"E305")])]});
            hole(context, id + "F5", {"style" : HoleStyle.SIMPLE, "holeDiameter" : 3 * mm, "endStyle" : HoleEndStyle.THROUGH, "locations" : qUnion([Q0, Q1, Q2, Q3]), "scope" : qUnion([Q4])});
        }
    });
